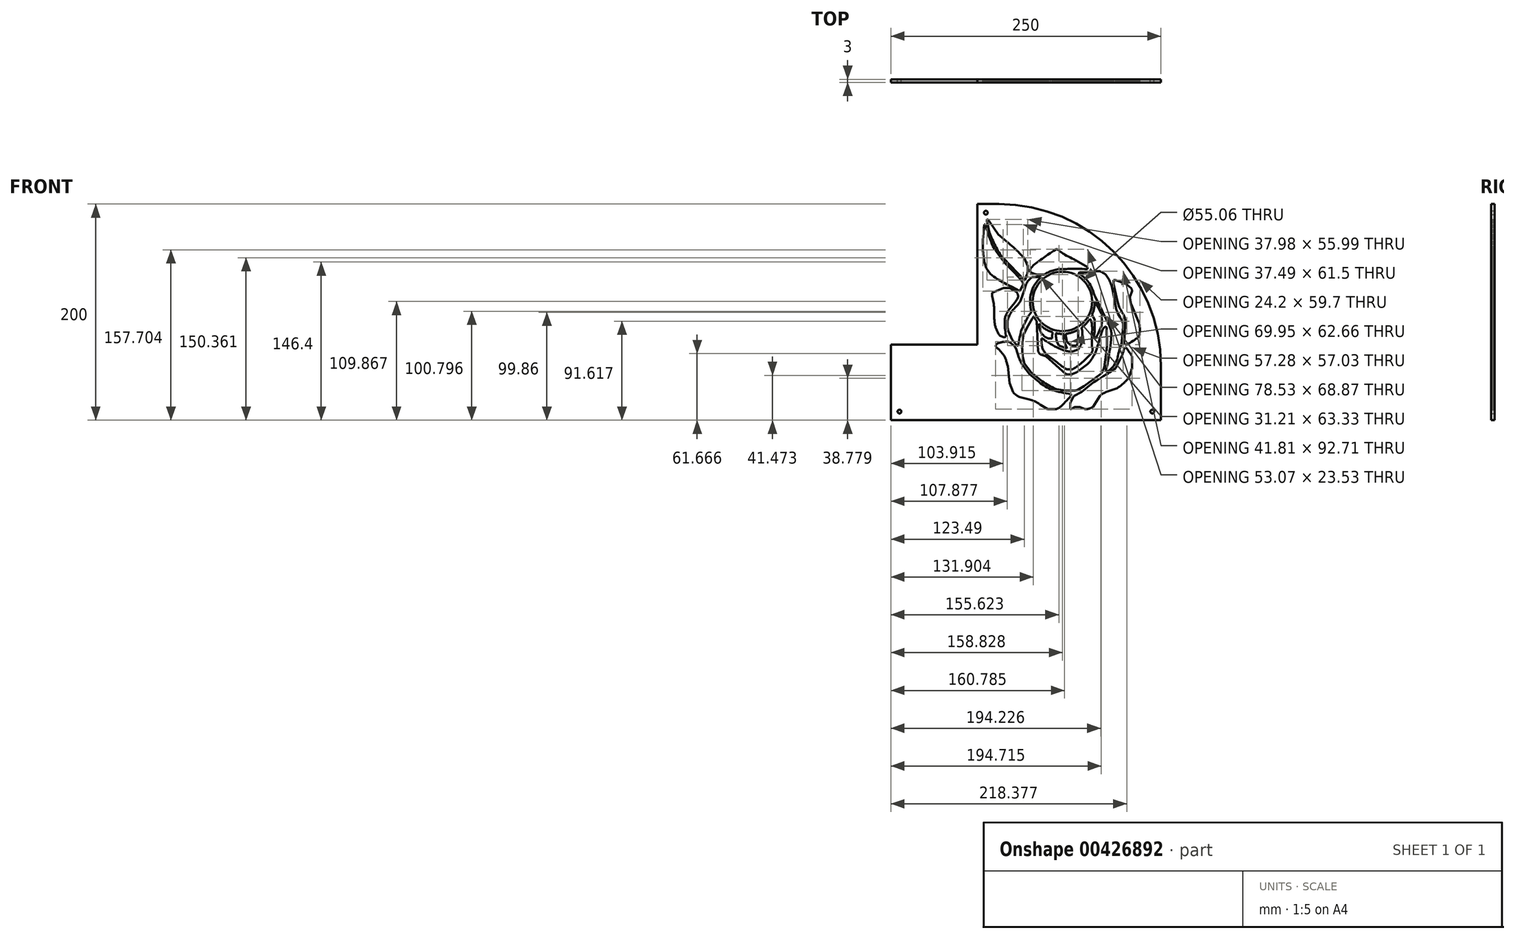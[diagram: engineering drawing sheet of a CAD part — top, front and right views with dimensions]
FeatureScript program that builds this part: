
annotation { "Feature Type Name" : "Feature", "Feature Type Description" : "" }
export const myFeature = defineFeature(function(context is Context, id is Id, definition is map)
    precondition{}
    {
        {
            var Q0;
            Q0=qCreatedBy(makeId("Front.planeOp"),FACE);
            var sketch = newSketch(context, id + "F0", { "sketchPlane" : qUnion([Q0])});
            skCircle(sketch, "E0", {"center": v(-37, 92) * mm, "radius": 1.75 * mm});
            skCircle(sketch, "E1", {"center": v(117, -92) * mm, "radius": 1.75 * mm});
            skCircle(sketch, "E2", {"center": v(-117, -92) * mm, "radius": 1.75 * mm});
            skArc(sketch, "E3", {"start": v(7.17, -3.9) * mm, "mid": v(8.49, -6.2) * mm, "end": v(10, -8.36) * mm});
            skArc(sketch, "E4", {"start": v(14.1, 32.46) * mm, "mid": v(4.86, 17.68) * mm, "end": v(5.4, 0.27) * mm});
            skArc(sketch, "E5", {"start": v(36.3, 39.77) * mm, "mid": v(26.32, 38.91) * mm, "end": v(17.19, 34.83) * mm});
            skArc(sketch, "E6", {"start": v(63.2, 15.94) * mm, "mid": v(57.98, 27.67) * mm, "end": v(48.32, 36.13) * mm});
            skArc(sketch, "E7", {"start": v(61.19, -2.44) * mm, "mid": v(63.17, 3.6) * mm, "end": v(63.83, 9.92) * mm});
            skArc(sketch, "E8", {"start": v(51.56, -14.33) * mm, "mid": v(55.76, -10.6) * mm, "end": v(59.19, -6.16) * mm});
            skArc(sketch, "E9", {"start": v(37.04, -19.96) * mm, "mid": v(42.76, -18.77) * mm, "end": v(48.14, -16.5) * mm});
            skArc(sketch, "E10", {"start": v(27.58, -19.48) * mm, "mid": v(31.5, -20.04) * mm, "end": v(35.45, -20.09) * mm});
            skArc(sketch, "E11", {"start": v(12.1, -10.82) * mm, "mid": v(17.92, -15.57) * mm, "end": v(24.74, -18.72) * mm});
            skLineSegment(sketch, "E12", {"start": v(-45, 100) * mm, "end": v(-25, 100) * mm});
            skLineSegment(sketch, "E13", {"start": v(-45, 100) * mm, "end": v(-45, -30) * mm});
            skLineSegment(sketch, "E14", {"start": v(-125, -30) * mm, "end": v(-45, -30) * mm});
            skLineSegment(sketch, "E15", {"start": v(-125, -100) * mm, "end": v(-125, -30) * mm});
            skLineSegment(sketch, "E16", {"start": v(-125, -100) * mm, "end": v(125, -100) * mm});
            skLineSegment(sketch, "E17", {"start": v(125, -100) * mm, "end": v(125, -50) * mm});
            skArc(sketch, "E18", {"start": v(125, -50) * mm, "mid": v(81.07, 56.07) * mm, "end": v(-25, 100) * mm});
            skLineSegment(sketch, "E19", {"start": v(-36.11, 85.7) * mm, "end": v(-35.91, 84.19) * mm});
            skLineSegment(sketch, "E20", {"start": v(-35.91, 84.19) * mm, "end": v(-35.68, 82.68) * mm});
            skLineSegment(sketch, "E21", {"start": v(-35.68, 82.68) * mm, "end": v(-35.43, 81.18) * mm});
            skLineSegment(sketch, "E22", {"start": v(-35.43, 81.18) * mm, "end": v(-35.14, 79.68) * mm});
            skLineSegment(sketch, "E23", {"start": v(-35.14, 79.68) * mm, "end": v(-34.83, 78.2) * mm});
            skLineSegment(sketch, "E24", {"start": v(-34.83, 78.2) * mm, "end": v(-34.49, 76.71) * mm});
            skLineSegment(sketch, "E25", {"start": v(-34.49, 76.71) * mm, "end": v(-34.11, 75.24) * mm});
            skLineSegment(sketch, "E26", {"start": v(-34.11, 75.24) * mm, "end": v(-33.7, 73.77) * mm});
            skLineSegment(sketch, "E27", {"start": v(-33.7, 73.77) * mm, "end": v(-32.43, 70.56) * mm});
            skLineSegment(sketch, "E28", {"start": v(-32.43, 70.56) * mm, "end": v(-31.78, 68.96) * mm});
            skLineSegment(sketch, "E29", {"start": v(-31.78, 68.96) * mm, "end": v(-31.11, 67.37) * mm});
            skLineSegment(sketch, "E30", {"start": v(-31.11, 67.37) * mm, "end": v(-30.43, 65.8) * mm});
            skLineSegment(sketch, "E31", {"start": v(-30.43, 65.8) * mm, "end": v(-29.72, 64.23) * mm});
            skLineSegment(sketch, "E32", {"start": v(-29.72, 64.23) * mm, "end": v(-28.99, 62.68) * mm});
            skLineSegment(sketch, "E33", {"start": v(-28.99, 62.68) * mm, "end": v(-28.23, 61.15) * mm});
            skLineSegment(sketch, "E34", {"start": v(-28.23, 61.15) * mm, "end": v(-27.44, 59.64) * mm});
            skLineSegment(sketch, "E35", {"start": v(-27.44, 59.64) * mm, "end": v(-26.62, 58.15) * mm});
            skLineSegment(sketch, "E36", {"start": v(-26.62, 58.15) * mm, "end": v(-25.76, 56.7) * mm});
            skLineSegment(sketch, "E37", {"start": v(-25.76, 56.7) * mm, "end": v(-24.86, 55.27) * mm});
            skLineSegment(sketch, "E38", {"start": v(-24.86, 55.27) * mm, "end": v(-23.93, 53.87) * mm});
            skLineSegment(sketch, "E39", {"start": v(-23.93, 53.87) * mm, "end": v(-22.94, 52.5) * mm});
            skLineSegment(sketch, "E40", {"start": v(-22.94, 52.5) * mm, "end": v(-22.44, 51.84) * mm});
            skLineSegment(sketch, "E41", {"start": v(-22.44, 51.84) * mm, "end": v(-21.91, 51.19) * mm});
            skLineSegment(sketch, "E42", {"start": v(-21.91, 51.19) * mm, "end": v(-21.38, 50.54) * mm});
            skLineSegment(sketch, "E43", {"start": v(-21.38, 50.54) * mm, "end": v(-20.84, 49.9) * mm});
            skLineSegment(sketch, "E44", {"start": v(-20.84, 49.9) * mm, "end": v(-1.54, 29.7) * mm});
            skLineSegment(sketch, "E45", {"start": v(-1.54, 29.7) * mm, "end": v(-0.73, 29.7) * mm});
            skLineSegment(sketch, "E46", {"start": v(-0.73, 29.7) * mm, "end": v(0.87, 34.3) * mm});
            skLineSegment(sketch, "E47", {"start": v(0.87, 34.3) * mm, "end": v(1.04, 34.79) * mm});
            skLineSegment(sketch, "E48", {"start": v(1.04, 34.79) * mm, "end": v(1.2, 35.28) * mm});
            skLineSegment(sketch, "E49", {"start": v(1.2, 35.28) * mm, "end": v(1.33, 35.78) * mm});
            skLineSegment(sketch, "E50", {"start": v(1.33, 35.78) * mm, "end": v(1.46, 36.3) * mm});
            skLineSegment(sketch, "E51", {"start": v(1.46, 36.3) * mm, "end": v(1.56, 36.8) * mm});
            skLineSegment(sketch, "E52", {"start": v(1.56, 36.8) * mm, "end": v(1.65, 37.32) * mm});
            skLineSegment(sketch, "E53", {"start": v(1.65, 37.32) * mm, "end": v(1.73, 37.84) * mm});
            skLineSegment(sketch, "E54", {"start": v(1.73, 37.84) * mm, "end": v(1.79, 38.36) * mm});
            skLineSegment(sketch, "E55", {"start": v(1.79, 38.36) * mm, "end": v(1.83, 38.89) * mm});
            skLineSegment(sketch, "E56", {"start": v(1.83, 38.89) * mm, "end": v(1.86, 39.41) * mm});
            skLineSegment(sketch, "E57", {"start": v(1.86, 39.41) * mm, "end": v(1.87, 39.94) * mm});
            skLineSegment(sketch, "E58", {"start": v(1.87, 39.94) * mm, "end": v(1.86, 40.47) * mm});
            skLineSegment(sketch, "E59", {"start": v(1.86, 40.47) * mm, "end": v(1.84, 41) * mm});
            skLineSegment(sketch, "E60", {"start": v(1.84, 41) * mm, "end": v(1.8, 41.52) * mm});
            skLineSegment(sketch, "E61", {"start": v(1.8, 41.52) * mm, "end": v(1.75, 42.04) * mm});
            skLineSegment(sketch, "E62", {"start": v(1.75, 42.04) * mm, "end": v(1.68, 42.56) * mm});
            skLineSegment(sketch, "E63", {"start": v(1.68, 42.56) * mm, "end": v(-1.54, 49.9) * mm});
            skLineSegment(sketch, "E64", {"start": v(-1.54, 49.9) * mm, "end": v(-2.92, 51.44) * mm});
            skLineSegment(sketch, "E65", {"start": v(-2.92, 51.44) * mm, "end": v(-4.32, 52.95) * mm});
            skLineSegment(sketch, "E66", {"start": v(-4.32, 52.95) * mm, "end": v(-5.75, 54.42) * mm});
            skLineSegment(sketch, "E67", {"start": v(-5.75, 54.42) * mm, "end": v(-7.2, 55.87) * mm});
            skLineSegment(sketch, "E68", {"start": v(-7.2, 55.87) * mm, "end": v(-8.67, 57.3) * mm});
            skLineSegment(sketch, "E69", {"start": v(-8.67, 57.3) * mm, "end": v(-10.16, 58.69) * mm});
            skLineSegment(sketch, "E70", {"start": v(-10.16, 58.69) * mm, "end": v(-11.67, 60.07) * mm});
            skLineSegment(sketch, "E71", {"start": v(-11.67, 60.07) * mm, "end": v(-13.19, 61.43) * mm});
            skLineSegment(sketch, "E72", {"start": v(-13.19, 61.43) * mm, "end": v(-14.72, 62.77) * mm});
            skLineSegment(sketch, "E73", {"start": v(-14.72, 62.77) * mm, "end": v(-16.27, 64.1) * mm});
            skLineSegment(sketch, "E74", {"start": v(-16.27, 64.1) * mm, "end": v(-19.39, 66.73) * mm});
            skLineSegment(sketch, "E75", {"start": v(-19.39, 66.73) * mm, "end": v(-25.66, 71.93) * mm});
            skLineSegment(sketch, "E76", {"start": v(-25.66, 71.93) * mm, "end": v(-33.7, 83.86) * mm});
            skLineSegment(sketch, "E77", {"start": v(-33.7, 83.86) * mm, "end": v(-34.12, 84.53) * mm});
            skLineSegment(sketch, "E78", {"start": v(-34.12, 84.53) * mm, "end": v(-34.34, 84.84) * mm});
            skLineSegment(sketch, "E79", {"start": v(-34.34, 84.84) * mm, "end": v(-34.6, 85.12) * mm});
            skLineSegment(sketch, "E80", {"start": v(-34.6, 85.12) * mm, "end": v(-34.73, 85.24) * mm});
            skLineSegment(sketch, "E81", {"start": v(-34.73, 85.24) * mm, "end": v(-34.88, 85.35) * mm});
            skLineSegment(sketch, "E82", {"start": v(-34.88, 85.35) * mm, "end": v(-35.04, 85.45) * mm});
            skLineSegment(sketch, "E83", {"start": v(-35.04, 85.45) * mm, "end": v(-35.22, 85.54) * mm});
            skLineSegment(sketch, "E84", {"start": v(-35.22, 85.54) * mm, "end": v(-35.41, 85.6) * mm});
            skLineSegment(sketch, "E85", {"start": v(-35.41, 85.6) * mm, "end": v(-35.63, 85.66) * mm});
            skLineSegment(sketch, "E86", {"start": v(-35.63, 85.66) * mm, "end": v(-35.86, 85.69) * mm});
            skLineSegment(sketch, "E87", {"start": v(-35.86, 85.69) * mm, "end": v(-36.11, 85.7) * mm});
            skLineSegment(sketch, "E88", {"start": v(-37.72, 81.11) * mm, "end": v(-38.52, 81.11) * mm});
            skLineSegment(sketch, "E89", {"start": v(-38.52, 81.11) * mm, "end": v(-39.33, 73.77) * mm});
            skLineSegment(sketch, "E90", {"start": v(-39.33, 73.77) * mm, "end": v(-39.58, 69.44) * mm});
            skLineSegment(sketch, "E91", {"start": v(-39.58, 69.44) * mm, "end": v(-39.68, 67.27) * mm});
            skLineSegment(sketch, "E92", {"start": v(-39.68, 67.27) * mm, "end": v(-39.77, 65.09) * mm});
            skLineSegment(sketch, "E93", {"start": v(-39.77, 65.09) * mm, "end": v(-39.82, 62.91) * mm});
            skLineSegment(sketch, "E94", {"start": v(-39.82, 62.91) * mm, "end": v(-39.83, 60.74) * mm});
            skLineSegment(sketch, "E95", {"start": v(-39.83, 60.74) * mm, "end": v(-39.8, 58.57) * mm});
            skLineSegment(sketch, "E96", {"start": v(-39.8, 58.57) * mm, "end": v(-39.7, 56.4) * mm});
            skLineSegment(sketch, "E97", {"start": v(-39.7, 56.4) * mm, "end": v(-39.64, 55.33) * mm});
            skLineSegment(sketch, "E98", {"start": v(-39.64, 55.33) * mm, "end": v(-39.55, 54.26) * mm});
            skLineSegment(sketch, "E99", {"start": v(-39.55, 54.26) * mm, "end": v(-39.45, 53.19) * mm});
            skLineSegment(sketch, "E100", {"start": v(-39.45, 53.19) * mm, "end": v(-39.33, 52.13) * mm});
            skLineSegment(sketch, "E101", {"start": v(-39.33, 52.13) * mm, "end": v(-39.2, 51.07) * mm});
            skLineSegment(sketch, "E102", {"start": v(-39.2, 51.07) * mm, "end": v(-39.03, 50) * mm});
            skLineSegment(sketch, "E103", {"start": v(-39.03, 50) * mm, "end": v(-38.85, 48.96) * mm});
            skLineSegment(sketch, "E104", {"start": v(-38.85, 48.96) * mm, "end": v(-38.65, 47.92) * mm});
            skLineSegment(sketch, "E105", {"start": v(-38.65, 47.92) * mm, "end": v(-38.42, 46.88) * mm});
            skLineSegment(sketch, "E106", {"start": v(-38.42, 46.88) * mm, "end": v(-38.17, 45.84) * mm});
            skLineSegment(sketch, "E107", {"start": v(-38.17, 45.84) * mm, "end": v(-37.9, 44.82) * mm});
            skLineSegment(sketch, "E108", {"start": v(-37.9, 44.82) * mm, "end": v(-37.6, 43.8) * mm});
            skLineSegment(sketch, "E109", {"start": v(-37.6, 43.8) * mm, "end": v(-37.27, 42.8) * mm});
            skLineSegment(sketch, "E110", {"start": v(-37.27, 42.8) * mm, "end": v(-36.91, 41.79) * mm});
            skLineSegment(sketch, "E111", {"start": v(-36.91, 41.79) * mm, "end": v(-36.53, 40.8) * mm});
            skLineSegment(sketch, "E112", {"start": v(-36.53, 40.8) * mm, "end": v(-36.11, 39.8) * mm});
            skLineSegment(sketch, "E113", {"start": v(-36.11, 39.8) * mm, "end": v(-32.9, 35.22) * mm});
            skLineSegment(sketch, "E114", {"start": v(-32.9, 35.22) * mm, "end": v(-31.3, 34.03) * mm});
            skLineSegment(sketch, "E115", {"start": v(-31.3, 34.03) * mm, "end": v(-29.67, 32.9) * mm});
            skLineSegment(sketch, "E116", {"start": v(-29.67, 32.9) * mm, "end": v(-28.03, 31.8) * mm});
            skLineSegment(sketch, "E117", {"start": v(-28.03, 31.8) * mm, "end": v(-26.36, 30.73) * mm});
            skLineSegment(sketch, "E118", {"start": v(-26.36, 30.73) * mm, "end": v(-24.68, 29.7) * mm});
            skLineSegment(sketch, "E119", {"start": v(-24.68, 29.7) * mm, "end": v(-22.98, 28.7) * mm});
            skLineSegment(sketch, "E120", {"start": v(-22.98, 28.7) * mm, "end": v(-21.27, 27.74) * mm});
            skLineSegment(sketch, "E121", {"start": v(-21.27, 27.74) * mm, "end": v(-19.55, 26.8) * mm});
            skLineSegment(sketch, "E122", {"start": v(-19.55, 26.8) * mm, "end": v(-17.81, 25.87) * mm});
            skLineSegment(sketch, "E123", {"start": v(-17.81, 25.87) * mm, "end": v(-16.07, 24.95) * mm});
            skLineSegment(sketch, "E124", {"start": v(-16.07, 24.95) * mm, "end": v(-12.57, 23.16) * mm});
            skLineSegment(sketch, "E125", {"start": v(-12.57, 23.16) * mm, "end": v(-9.06, 21.4) * mm});
            skLineSegment(sketch, "E126", {"start": v(-9.06, 21.4) * mm, "end": v(-5.56, 19.61) * mm});
            skLineSegment(sketch, "E127", {"start": v(-5.56, 19.61) * mm, "end": v(-2.34, 26.04) * mm});
            skLineSegment(sketch, "E128", {"start": v(-2.34, 26.04) * mm, "end": v(-3.15, 27.87) * mm});
            skLineSegment(sketch, "E129", {"start": v(-3.15, 27.87) * mm, "end": v(-3.98, 28.93) * mm});
            skLineSegment(sketch, "E130", {"start": v(-3.98, 28.93) * mm, "end": v(-4.82, 29.97) * mm});
            skLineSegment(sketch, "E131", {"start": v(-4.82, 29.97) * mm, "end": v(-6.53, 32.03) * mm});
            skLineSegment(sketch, "E132", {"start": v(-6.53, 32.03) * mm, "end": v(-8.29, 34.04) * mm});
            skLineSegment(sketch, "E133", {"start": v(-8.29, 34.04) * mm, "end": v(-10.08, 36.01) * mm});
            skLineSegment(sketch, "E134", {"start": v(-10.08, 36.01) * mm, "end": v(-11.9, 37.94) * mm});
            skLineSegment(sketch, "E135", {"start": v(-11.9, 37.94) * mm, "end": v(-13.78, 39.83) * mm});
            skLineSegment(sketch, "E136", {"start": v(-13.78, 39.83) * mm, "end": v(-15.68, 41.67) * mm});
            skLineSegment(sketch, "E137", {"start": v(-15.68, 41.67) * mm, "end": v(-17.62, 43.48) * mm});
            skLineSegment(sketch, "E138", {"start": v(-17.62, 43.48) * mm, "end": v(-18.5, 44.5) * mm});
            skLineSegment(sketch, "E139", {"start": v(-18.5, 44.5) * mm, "end": v(-19.36, 45.52) * mm});
            skLineSegment(sketch, "E140", {"start": v(-19.36, 45.52) * mm, "end": v(-20.22, 46.55) * mm});
            skLineSegment(sketch, "E141", {"start": v(-20.22, 46.55) * mm, "end": v(-21.06, 47.6) * mm});
            skLineSegment(sketch, "E142", {"start": v(-21.06, 47.6) * mm, "end": v(-22.72, 49.73) * mm});
            skLineSegment(sketch, "E143", {"start": v(-22.72, 49.73) * mm, "end": v(-24.34, 51.9) * mm});
            skLineSegment(sketch, "E144", {"start": v(-24.34, 51.9) * mm, "end": v(-25.92, 54.1) * mm});
            skLineSegment(sketch, "E145", {"start": v(-25.92, 54.1) * mm, "end": v(-27.47, 56.34) * mm});
            skLineSegment(sketch, "E146", {"start": v(-27.47, 56.34) * mm, "end": v(-29, 58.61) * mm});
            skLineSegment(sketch, "E147", {"start": v(-29, 58.61) * mm, "end": v(-30.48, 60.92) * mm});
            skLineSegment(sketch, "E148", {"start": v(-30.48, 60.92) * mm, "end": v(-31.43, 63.14) * mm});
            skLineSegment(sketch, "E149", {"start": v(-31.43, 63.14) * mm, "end": v(-32.32, 65.39) * mm});
            skLineSegment(sketch, "E150", {"start": v(-32.32, 65.39) * mm, "end": v(-33.17, 67.66) * mm});
            skLineSegment(sketch, "E151", {"start": v(-33.17, 67.66) * mm, "end": v(-33.98, 69.95) * mm});
            skLineSegment(sketch, "E152", {"start": v(-33.98, 69.95) * mm, "end": v(-34.76, 72.26) * mm});
            skLineSegment(sketch, "E153", {"start": v(-34.76, 72.26) * mm, "end": v(-35.5, 74.59) * mm});
            skLineSegment(sketch, "E154", {"start": v(-35.5, 74.59) * mm, "end": v(-36.22, 76.92) * mm});
            skLineSegment(sketch, "E155", {"start": v(-36.22, 76.92) * mm, "end": v(-36.92, 79.27) * mm});
            skLineSegment(sketch, "E156", {"start": v(-36.92, 79.27) * mm, "end": v(-37.72, 81.11) * mm});
            skLineSegment(sketch, "E157", {"start": v(36.3, 39.77) * mm, "end": v(37.58, 39.94) * mm});
            skLineSegment(sketch, "E158", {"start": v(37.58, 39.94) * mm, "end": v(38.87, 40.06) * mm});
            skLineSegment(sketch, "E159", {"start": v(38.87, 40.06) * mm, "end": v(40.16, 40.15) * mm});
            skLineSegment(sketch, "E160", {"start": v(40.16, 40.15) * mm, "end": v(41.46, 40.2) * mm});
            skLineSegment(sketch, "E161", {"start": v(41.46, 40.2) * mm, "end": v(42.76, 40.23) * mm});
            skLineSegment(sketch, "E162", {"start": v(42.76, 40.23) * mm, "end": v(44.07, 40.23) * mm});
            skLineSegment(sketch, "E163", {"start": v(44.07, 40.23) * mm, "end": v(45.37, 40.2) * mm});
            skLineSegment(sketch, "E164", {"start": v(45.37, 40.2) * mm, "end": v(46.68, 40.17) * mm});
            skLineSegment(sketch, "E165", {"start": v(46.68, 40.17) * mm, "end": v(49.3, 40.06) * mm});
            skLineSegment(sketch, "E166", {"start": v(49.3, 40.06) * mm, "end": v(51.93, 39.94) * mm});
            skLineSegment(sketch, "E167", {"start": v(51.93, 39.94) * mm, "end": v(54.55, 39.85) * mm});
            skLineSegment(sketch, "E168", {"start": v(54.55, 39.85) * mm, "end": v(55.85, 39.82) * mm});
            skLineSegment(sketch, "E169", {"start": v(55.85, 39.82) * mm, "end": v(57.16, 39.8) * mm});
            skLineSegment(sketch, "E170", {"start": v(57.16, 39.8) * mm, "end": v(57.16, 41.64) * mm});
            skLineSegment(sketch, "E171", {"start": v(57.16, 41.64) * mm, "end": v(44.3, 48.98) * mm});
            skLineSegment(sketch, "E172", {"start": v(44.3, 48.98) * mm, "end": v(42.63, 49.76) * mm});
            skLineSegment(sketch, "E173", {"start": v(42.63, 49.76) * mm, "end": v(40.97, 50.56) * mm});
            skLineSegment(sketch, "E174", {"start": v(40.97, 50.56) * mm, "end": v(39.33, 51.4) * mm});
            skLineSegment(sketch, "E175", {"start": v(39.33, 51.4) * mm, "end": v(37.7, 52.26) * mm});
            skLineSegment(sketch, "E176", {"start": v(37.7, 52.26) * mm, "end": v(36.1, 53.19) * mm});
            skLineSegment(sketch, "E177", {"start": v(36.1, 53.19) * mm, "end": v(35.3, 53.67) * mm});
            skLineSegment(sketch, "E178", {"start": v(35.3, 53.67) * mm, "end": v(34.52, 54.17) * mm});
            skLineSegment(sketch, "E179", {"start": v(34.52, 54.17) * mm, "end": v(33.73, 54.68) * mm});
            skLineSegment(sketch, "E180", {"start": v(33.73, 54.68) * mm, "end": v(32.96, 55.21) * mm});
            skLineSegment(sketch, "E181", {"start": v(32.96, 55.21) * mm, "end": v(32.19, 55.76) * mm});
            skLineSegment(sketch, "E182", {"start": v(32.19, 55.76) * mm, "end": v(31.43, 56.33) * mm});
            skLineSegment(sketch, "E183", {"start": v(31.43, 56.33) * mm, "end": v(31.1, 56.68) * mm});
            skLineSegment(sketch, "E184", {"start": v(31.1, 56.68) * mm, "end": v(30.77, 57.02) * mm});
            skLineSegment(sketch, "E185", {"start": v(30.77, 57.02) * mm, "end": v(30.42, 57.33) * mm});
            skLineSegment(sketch, "E186", {"start": v(30.42, 57.33) * mm, "end": v(30.05, 57.6) * mm});
            skLineSegment(sketch, "E187", {"start": v(30.05, 57.6) * mm, "end": v(29.85, 57.73) * mm});
            skLineSegment(sketch, "E188", {"start": v(29.85, 57.73) * mm, "end": v(29.65, 57.84) * mm});
            skLineSegment(sketch, "E189", {"start": v(29.65, 57.84) * mm, "end": v(29.43, 57.93) * mm});
            skLineSegment(sketch, "E190", {"start": v(29.43, 57.93) * mm, "end": v(29.2, 58.01) * mm});
            skLineSegment(sketch, "E191", {"start": v(29.2, 58.01) * mm, "end": v(28.98, 58.08) * mm});
            skLineSegment(sketch, "E192", {"start": v(28.98, 58.08) * mm, "end": v(28.73, 58.12) * mm});
            skLineSegment(sketch, "E193", {"start": v(28.73, 58.12) * mm, "end": v(28.48, 58.15) * mm});
            skLineSegment(sketch, "E194", {"start": v(28.48, 58.15) * mm, "end": v(28.21, 58.16) * mm});
            skLineSegment(sketch, "E195", {"start": v(28.21, 58.16) * mm, "end": v(25.51, 56.5) * mm});
            skLineSegment(sketch, "E196", {"start": v(25.51, 56.5) * mm, "end": v(22.83, 54.8) * mm});
            skLineSegment(sketch, "E197", {"start": v(22.83, 54.8) * mm, "end": v(20.18, 53.04) * mm});
            skLineSegment(sketch, "E198", {"start": v(20.18, 53.04) * mm, "end": v(17.55, 51.24) * mm});
            skLineSegment(sketch, "E199", {"start": v(17.55, 51.24) * mm, "end": v(16.24, 50.32) * mm});
            skLineSegment(sketch, "E200", {"start": v(16.24, 50.32) * mm, "end": v(14.94, 49.4) * mm});
            skLineSegment(sketch, "E201", {"start": v(14.94, 49.4) * mm, "end": v(13.65, 48.45) * mm});
            skLineSegment(sketch, "E202", {"start": v(13.65, 48.45) * mm, "end": v(12.36, 47.48) * mm});
            skLineSegment(sketch, "E203", {"start": v(12.36, 47.48) * mm, "end": v(11.09, 46.5) * mm});
            skLineSegment(sketch, "E204", {"start": v(11.09, 46.5) * mm, "end": v(9.82, 45.51) * mm});
            skLineSegment(sketch, "E205", {"start": v(9.82, 45.51) * mm, "end": v(8.56, 44.5) * mm});
            skLineSegment(sketch, "E206", {"start": v(8.56, 44.5) * mm, "end": v(7.3, 43.48) * mm});
            skLineSegment(sketch, "E207", {"start": v(7.3, 43.48) * mm, "end": v(4.09, 39.8) * mm});
            skLineSegment(sketch, "E208", {"start": v(4.09, 39.8) * mm, "end": v(4.09, 37.05) * mm});
            skLineSegment(sketch, "E209", {"start": v(4.09, 37.05) * mm, "end": v(8.11, 35.22) * mm});
            skLineSegment(sketch, "E210", {"start": v(8.11, 35.22) * mm, "end": v(9.24, 35) * mm});
            skLineSegment(sketch, "E211", {"start": v(9.24, 35) * mm, "end": v(10.37, 34.84) * mm});
            skLineSegment(sketch, "E212", {"start": v(10.37, 34.84) * mm, "end": v(11.5, 34.72) * mm});
            skLineSegment(sketch, "E213", {"start": v(11.5, 34.72) * mm, "end": v(12.64, 34.66) * mm});
            skLineSegment(sketch, "E214", {"start": v(12.64, 34.66) * mm, "end": v(13.77, 34.64) * mm});
            skLineSegment(sketch, "E215", {"start": v(13.77, 34.64) * mm, "end": v(14.91, 34.66) * mm});
            skLineSegment(sketch, "E216", {"start": v(14.91, 34.66) * mm, "end": v(16.05, 34.73) * mm});
            skLineSegment(sketch, "E217", {"start": v(16.05, 34.73) * mm, "end": v(17.19, 34.83) * mm});
            skLineSegment(sketch, "E218", {"start": v(63.2, 15.94) * mm, "end": v(64.4, 14.1) * mm});
            skLineSegment(sketch, "E219", {"start": v(64.4, 14.1) * mm, "end": v(77.26, -12.51) * mm});
            skLineSegment(sketch, "E220", {"start": v(77.26, -12.51) * mm, "end": v(78.87, -17.1) * mm});
            skLineSegment(sketch, "E221", {"start": v(78.87, -17.1) * mm, "end": v(79, -18.12) * mm});
            skLineSegment(sketch, "E222", {"start": v(79, -18.12) * mm, "end": v(79.07, -19.15) * mm});
            skLineSegment(sketch, "E223", {"start": v(79.07, -19.15) * mm, "end": v(79.1, -20.18) * mm});
            skLineSegment(sketch, "E224", {"start": v(79.1, -20.18) * mm, "end": v(79.1, -21.22) * mm});
            skLineSegment(sketch, "E225", {"start": v(79.1, -21.22) * mm, "end": v(79.07, -22.26) * mm});
            skLineSegment(sketch, "E226", {"start": v(79.07, -22.26) * mm, "end": v(79.01, -23.3) * mm});
            skLineSegment(sketch, "E227", {"start": v(79.01, -23.3) * mm, "end": v(78.87, -25.36) * mm});
            skLineSegment(sketch, "E228", {"start": v(78.87, -25.36) * mm, "end": v(78.2, -30.9) * mm});
            skLineSegment(sketch, "E229", {"start": v(78.2, -30.9) * mm, "end": v(77.84, -33.66) * mm});
            skLineSegment(sketch, "E230", {"start": v(77.84, -33.66) * mm, "end": v(77.47, -36.41) * mm});
            skLineSegment(sketch, "E231", {"start": v(77.47, -36.41) * mm, "end": v(77.06, -39.17) * mm});
            skLineSegment(sketch, "E232", {"start": v(77.06, -39.17) * mm, "end": v(76.63, -41.92) * mm});
            skLineSegment(sketch, "E233", {"start": v(76.63, -41.92) * mm, "end": v(76.16, -44.66) * mm});
            skLineSegment(sketch, "E234", {"start": v(76.16, -44.66) * mm, "end": v(75.65, -47.4) * mm});
            skLineSegment(sketch, "E235", {"start": v(75.65, -47.4) * mm, "end": v(74.04, -52.9) * mm});
            skLineSegment(sketch, "E236", {"start": v(74.04, -52.9) * mm, "end": v(74.04, -54.74) * mm});
            skLineSegment(sketch, "E237", {"start": v(74.04, -54.74) * mm, "end": v(74.46, -54.73) * mm});
            skLineSegment(sketch, "E238", {"start": v(74.46, -54.73) * mm, "end": v(74.88, -54.7) * mm});
            skLineSegment(sketch, "E239", {"start": v(74.88, -54.7) * mm, "end": v(75.3, -54.65) * mm});
            skLineSegment(sketch, "E240", {"start": v(75.3, -54.65) * mm, "end": v(75.71, -54.57) * mm});
            skLineSegment(sketch, "E241", {"start": v(75.71, -54.57) * mm, "end": v(76.12, -54.45) * mm});
            skLineSegment(sketch, "E242", {"start": v(76.12, -54.45) * mm, "end": v(76.51, -54.3) * mm});
            skLineSegment(sketch, "E243", {"start": v(76.51, -54.3) * mm, "end": v(76.9, -54.08) * mm});
            skLineSegment(sketch, "E244", {"start": v(76.9, -54.08) * mm, "end": v(77.26, -53.82) * mm});
            skLineSegment(sketch, "E245", {"start": v(77.26, -53.82) * mm, "end": v(81.28, -50.15) * mm});
            skLineSegment(sketch, "E246", {"start": v(81.28, -50.15) * mm, "end": v(84.5, -43.72) * mm});
            skLineSegment(sketch, "E247", {"start": v(84.5, -43.72) * mm, "end": v(84.88, -41.96) * mm});
            skLineSegment(sketch, "E248", {"start": v(84.88, -41.96) * mm, "end": v(85.29, -40.2) * mm});
            skLineSegment(sketch, "E249", {"start": v(85.29, -40.2) * mm, "end": v(85.71, -38.45) * mm});
            skLineSegment(sketch, "E250", {"start": v(85.71, -38.45) * mm, "end": v(86.17, -36.71) * mm});
            skLineSegment(sketch, "E251", {"start": v(86.17, -36.71) * mm, "end": v(86.67, -34.99) * mm});
            skLineSegment(sketch, "E252", {"start": v(86.67, -34.99) * mm, "end": v(86.94, -34.13) * mm});
            skLineSegment(sketch, "E253", {"start": v(86.94, -34.13) * mm, "end": v(87.22, -33.29) * mm});
            skLineSegment(sketch, "E254", {"start": v(87.22, -33.29) * mm, "end": v(87.52, -32.44) * mm});
            skLineSegment(sketch, "E255", {"start": v(87.52, -32.44) * mm, "end": v(87.83, -31.6) * mm});
            skLineSegment(sketch, "E256", {"start": v(87.83, -31.6) * mm, "end": v(88.17, -30.78) * mm});
            skLineSegment(sketch, "E257", {"start": v(88.17, -30.78) * mm, "end": v(88.51, -29.95) * mm});
            skLineSegment(sketch, "E258", {"start": v(88.51, -29.95) * mm, "end": v(90.12, -13.43) * mm});
            skLineSegment(sketch, "E259", {"start": v(90.12, -13.43) * mm, "end": v(90.13, -12.97) * mm});
            skLineSegment(sketch, "E260", {"start": v(90.13, -12.97) * mm, "end": v(90.12, -12.52) * mm});
            skLineSegment(sketch, "E261", {"start": v(90.12, -12.52) * mm, "end": v(90.09, -12.07) * mm});
            skLineSegment(sketch, "E262", {"start": v(90.09, -12.07) * mm, "end": v(90.03, -11.62) * mm});
            skLineSegment(sketch, "E263", {"start": v(90.03, -11.62) * mm, "end": v(89.96, -11.18) * mm});
            skLineSegment(sketch, "E264", {"start": v(89.96, -11.18) * mm, "end": v(89.88, -10.74) * mm});
            skLineSegment(sketch, "E265", {"start": v(89.88, -10.74) * mm, "end": v(89.77, -10.3) * mm});
            skLineSegment(sketch, "E266", {"start": v(89.77, -10.3) * mm, "end": v(89.65, -9.86) * mm});
            skLineSegment(sketch, "E267", {"start": v(89.65, -9.86) * mm, "end": v(89.37, -8.99) * mm});
            skLineSegment(sketch, "E268", {"start": v(89.37, -8.99) * mm, "end": v(89.04, -8.13) * mm});
            skLineSegment(sketch, "E269", {"start": v(89.04, -8.13) * mm, "end": v(88.66, -7.27) * mm});
            skLineSegment(sketch, "E270", {"start": v(88.66, -7.27) * mm, "end": v(88.24, -6.42) * mm});
            skLineSegment(sketch, "E271", {"start": v(88.24, -6.42) * mm, "end": v(87.8, -5.57) * mm});
            skLineSegment(sketch, "E272", {"start": v(87.8, -5.57) * mm, "end": v(87.33, -4.73) * mm});
            skLineSegment(sketch, "E273", {"start": v(87.33, -4.73) * mm, "end": v(86.36, -3.05) * mm});
            skLineSegment(sketch, "E274", {"start": v(86.36, -3.05) * mm, "end": v(85.4, -1.36) * mm});
            skLineSegment(sketch, "E275", {"start": v(85.4, -1.36) * mm, "end": v(84.94, -0.51) * mm});
            skLineSegment(sketch, "E276", {"start": v(84.94, -0.51) * mm, "end": v(84.5, 0.34) * mm});
            skLineSegment(sketch, "E277", {"start": v(84.5, 0.34) * mm, "end": v(83.7, 2.17) * mm});
            skLineSegment(sketch, "E278", {"start": v(83.7, 2.17) * mm, "end": v(80.47, 19.61) * mm});
            skLineSegment(sketch, "E279", {"start": v(80.47, 19.61) * mm, "end": v(79.8, 22.19) * mm});
            skLineSegment(sketch, "E280", {"start": v(79.8, 22.19) * mm, "end": v(79.45, 23.47) * mm});
            skLineSegment(sketch, "E281", {"start": v(79.45, 23.47) * mm, "end": v(79.07, 24.74) * mm});
            skLineSegment(sketch, "E282", {"start": v(79.07, 24.74) * mm, "end": v(78.67, 26) * mm});
            skLineSegment(sketch, "E283", {"start": v(78.67, 26) * mm, "end": v(78.24, 27.25) * mm});
            skLineSegment(sketch, "E284", {"start": v(78.24, 27.25) * mm, "end": v(77.77, 28.49) * mm});
            skLineSegment(sketch, "E285", {"start": v(77.77, 28.49) * mm, "end": v(77.26, 29.7) * mm});
            skLineSegment(sketch, "E286", {"start": v(77.26, 29.7) * mm, "end": v(74.04, 34.3) * mm});
            skLineSegment(sketch, "E287", {"start": v(74.04, 34.3) * mm, "end": v(73.75, 34.62) * mm});
            skLineSegment(sketch, "E288", {"start": v(73.75, 34.62) * mm, "end": v(73.45, 34.92) * mm});
            skLineSegment(sketch, "E289", {"start": v(73.45, 34.92) * mm, "end": v(73.13, 35.2) * mm});
            skLineSegment(sketch, "E290", {"start": v(73.13, 35.2) * mm, "end": v(72.8, 35.48) * mm});
            skLineSegment(sketch, "E291", {"start": v(72.8, 35.48) * mm, "end": v(72.47, 35.73) * mm});
            skLineSegment(sketch, "E292", {"start": v(72.47, 35.73) * mm, "end": v(72.13, 35.98) * mm});
            skLineSegment(sketch, "E293", {"start": v(72.13, 35.98) * mm, "end": v(71.43, 36.43) * mm});
            skLineSegment(sketch, "E294", {"start": v(71.43, 36.43) * mm, "end": v(70.7, 36.85) * mm});
            skLineSegment(sketch, "E295", {"start": v(70.7, 36.85) * mm, "end": v(69.95, 37.24) * mm});
            skLineSegment(sketch, "E296", {"start": v(69.95, 37.24) * mm, "end": v(69.19, 37.61) * mm});
            skLineSegment(sketch, "E297", {"start": v(69.19, 37.61) * mm, "end": v(68.41, 37.97) * mm});
            skLineSegment(sketch, "E298", {"start": v(68.41, 37.97) * mm, "end": v(63.59, 37.97) * mm});
            skLineSegment(sketch, "E299", {"start": v(63.59, 37.97) * mm, "end": v(61.7, 37.62) * mm});
            skLineSegment(sketch, "E300", {"start": v(61.7, 37.62) * mm, "end": v(59.8, 37.28) * mm});
            skLineSegment(sketch, "E301", {"start": v(59.8, 37.28) * mm, "end": v(57.9, 36.97) * mm});
            skLineSegment(sketch, "E302", {"start": v(57.9, 36.97) * mm, "end": v(56, 36.7) * mm});
            skLineSegment(sketch, "E303", {"start": v(56, 36.7) * mm, "end": v(54.09, 36.46) * mm});
            skLineSegment(sketch, "E304", {"start": v(54.09, 36.46) * mm, "end": v(53.13, 36.37) * mm});
            skLineSegment(sketch, "E305", {"start": v(53.13, 36.37) * mm, "end": v(52.17, 36.29) * mm});
            skLineSegment(sketch, "E306", {"start": v(52.17, 36.29) * mm, "end": v(51.21, 36.22) * mm});
            skLineSegment(sketch, "E307", {"start": v(51.21, 36.22) * mm, "end": v(50.25, 36.17) * mm});
            skLineSegment(sketch, "E308", {"start": v(50.25, 36.17) * mm, "end": v(49.29, 36.14) * mm});
            skLineSegment(sketch, "E309", {"start": v(49.29, 36.14) * mm, "end": v(48.32, 36.13) * mm});
            skLineSegment(sketch, "E310", {"start": v(14.1, 32.46) * mm, "end": v(5.7, 32.46) * mm});
            skLineSegment(sketch, "E311", {"start": v(5.7, 32.46) * mm, "end": v(1.68, 28.8) * mm});
            skLineSegment(sketch, "E312", {"start": v(1.68, 28.8) * mm, "end": v(1.15, 27.84) * mm});
            skLineSegment(sketch, "E313", {"start": v(1.15, 27.84) * mm, "end": v(0.68, 26.85) * mm});
            skLineSegment(sketch, "E314", {"start": v(0.68, 26.85) * mm, "end": v(0.24, 25.84) * mm});
            skLineSegment(sketch, "E315", {"start": v(0.24, 25.84) * mm, "end": v(-0.16, 24.8) * mm});
            skLineSegment(sketch, "E316", {"start": v(-0.16, 24.8) * mm, "end": v(-0.54, 23.76) * mm});
            skLineSegment(sketch, "E317", {"start": v(-0.54, 23.76) * mm, "end": v(-0.89, 22.7) * mm});
            skLineSegment(sketch, "E318", {"start": v(-0.89, 22.7) * mm, "end": v(-1.22, 21.61) * mm});
            skLineSegment(sketch, "E319", {"start": v(-1.22, 21.61) * mm, "end": v(-1.54, 20.53) * mm});
            skLineSegment(sketch, "E320", {"start": v(-1.54, 20.53) * mm, "end": v(-4.75, 10.43) * mm});
            skLineSegment(sketch, "E321", {"start": v(-4.75, 10.43) * mm, "end": v(-5.57, 9.3) * mm});
            skLineSegment(sketch, "E322", {"start": v(-5.57, 9.3) * mm, "end": v(-6.4, 8.2) * mm});
            skLineSegment(sketch, "E323", {"start": v(-6.4, 8.2) * mm, "end": v(-7.27, 7.13) * mm});
            skLineSegment(sketch, "E324", {"start": v(-7.27, 7.13) * mm, "end": v(-8.16, 6.09) * mm});
            skLineSegment(sketch, "E325", {"start": v(-8.16, 6.09) * mm, "end": v(-9.08, 5.07) * mm});
            skLineSegment(sketch, "E326", {"start": v(-9.08, 5.07) * mm, "end": v(-10.02, 4.08) * mm});
            skLineSegment(sketch, "E327", {"start": v(-10.02, 4.08) * mm, "end": v(-11, 3.11) * mm});
            skLineSegment(sketch, "E328", {"start": v(-11, 3.11) * mm, "end": v(-12, 2.17) * mm});
            skLineSegment(sketch, "E329", {"start": v(-12, 2.17) * mm, "end": v(-12.71, 1.12) * mm});
            skLineSegment(sketch, "E330", {"start": v(-12.71, 1.12) * mm, "end": v(-13.4, 0.04) * mm});
            skLineSegment(sketch, "E331", {"start": v(-13.4, 0.04) * mm, "end": v(-14.06, -1.06) * mm});
            skLineSegment(sketch, "E332", {"start": v(-14.06, -1.06) * mm, "end": v(-14.69, -2.19) * mm});
            skLineSegment(sketch, "E333", {"start": v(-14.69, -2.19) * mm, "end": v(-15.28, -3.35) * mm});
            skLineSegment(sketch, "E334", {"start": v(-15.28, -3.35) * mm, "end": v(-15.83, -4.53) * mm});
            skLineSegment(sketch, "E335", {"start": v(-15.83, -4.53) * mm, "end": v(-16.35, -5.75) * mm});
            skLineSegment(sketch, "E336", {"start": v(-16.35, -5.75) * mm, "end": v(-16.82, -7) * mm});
            skLineSegment(sketch, "E337", {"start": v(-16.82, -7) * mm, "end": v(-16.91, -7.7) * mm});
            skLineSegment(sketch, "E338", {"start": v(-16.91, -7.7) * mm, "end": v(-17, -8.39) * mm});
            skLineSegment(sketch, "E339", {"start": v(-17, -8.39) * mm, "end": v(-17.05, -9.08) * mm});
            skLineSegment(sketch, "E340", {"start": v(-17.05, -9.08) * mm, "end": v(-17.1, -9.78) * mm});
            skLineSegment(sketch, "E341", {"start": v(-17.1, -9.78) * mm, "end": v(-17.11, -10.48) * mm});
            skLineSegment(sketch, "E342", {"start": v(-17.11, -10.48) * mm, "end": v(-17.11, -11.18) * mm});
            skLineSegment(sketch, "E343", {"start": v(-17.11, -11.18) * mm, "end": v(-17.1, -11.88) * mm});
            skLineSegment(sketch, "E344", {"start": v(-17.1, -11.88) * mm, "end": v(-17.06, -12.58) * mm});
            skLineSegment(sketch, "E345", {"start": v(-17.06, -12.58) * mm, "end": v(-17, -13.28) * mm});
            skLineSegment(sketch, "E346", {"start": v(-17, -13.28) * mm, "end": v(-16.92, -13.97) * mm});
            skLineSegment(sketch, "E347", {"start": v(-16.92, -13.97) * mm, "end": v(-16.82, -14.66) * mm});
            skLineSegment(sketch, "E348", {"start": v(-16.82, -14.66) * mm, "end": v(-16.7, -15.35) * mm});
            skLineSegment(sketch, "E349", {"start": v(-16.7, -15.35) * mm, "end": v(-16.56, -16.03) * mm});
            skLineSegment(sketch, "E350", {"start": v(-16.56, -16.03) * mm, "end": v(-16.4, -16.7) * mm});
            skLineSegment(sketch, "E351", {"start": v(-16.4, -16.7) * mm, "end": v(-16.22, -17.36) * mm});
            skLineSegment(sketch, "E352", {"start": v(-16.22, -17.36) * mm, "end": v(-16.01, -18.02) * mm});
            skLineSegment(sketch, "E353", {"start": v(-16.01, -18.02) * mm, "end": v(-12.8, -25.36) * mm});
            skLineSegment(sketch, "E354", {"start": v(-12.8, -25.36) * mm, "end": v(-7.97, -30.87) * mm});
            skLineSegment(sketch, "E355", {"start": v(-7.97, -30.87) * mm, "end": v(-7.17, -30.87) * mm});
            skLineSegment(sketch, "E356", {"start": v(-7.17, -30.87) * mm, "end": v(-6.5, -27.16) * mm});
            skLineSegment(sketch, "E357", {"start": v(-6.5, -27.16) * mm, "end": v(-6.14, -25.32) * mm});
            skLineSegment(sketch, "E358", {"start": v(-6.14, -25.32) * mm, "end": v(-5.76, -23.48) * mm});
            skLineSegment(sketch, "E359", {"start": v(-5.76, -23.48) * mm, "end": v(-5.36, -21.64) * mm});
            skLineSegment(sketch, "E360", {"start": v(-5.36, -21.64) * mm, "end": v(-4.92, -19.81) * mm});
            skLineSegment(sketch, "E361", {"start": v(-4.92, -19.81) * mm, "end": v(-4.46, -18) * mm});
            skLineSegment(sketch, "E362", {"start": v(-4.46, -18) * mm, "end": v(-3.95, -16.18) * mm});
            skLineSegment(sketch, "E363", {"start": v(-3.95, -16.18) * mm, "end": v(2.48, -3.33) * mm});
            skLineSegment(sketch, "E364", {"start": v(2.48, -3.33) * mm, "end": v(3.93, -1.52) * mm});
            skLineSegment(sketch, "E365", {"start": v(3.93, -1.52) * mm, "end": v(5.4, 0.27) * mm});
            skLineSegment(sketch, "E366", {"start": v(81.28, 29.7) * mm, "end": v(81.28, 26.04) * mm});
            skLineSegment(sketch, "E367", {"start": v(81.28, 26.04) * mm, "end": v(84.5, 10.43) * mm});
            skLineSegment(sketch, "E368", {"start": v(84.5, 10.43) * mm, "end": v(85.14, 8.3) * mm});
            skLineSegment(sketch, "E369", {"start": v(85.14, 8.3) * mm, "end": v(85.48, 7.24) * mm});
            skLineSegment(sketch, "E370", {"start": v(85.48, 7.24) * mm, "end": v(85.85, 6.2) * mm});
            skLineSegment(sketch, "E371", {"start": v(85.85, 6.2) * mm, "end": v(86.25, 5.16) * mm});
            skLineSegment(sketch, "E372", {"start": v(86.25, 5.16) * mm, "end": v(86.7, 4.14) * mm});
            skLineSegment(sketch, "E373", {"start": v(86.7, 4.14) * mm, "end": v(87.18, 3.15) * mm});
            skLineSegment(sketch, "E374", {"start": v(87.18, 3.15) * mm, "end": v(87.44, 2.66) * mm});
            skLineSegment(sketch, "E375", {"start": v(87.44, 2.66) * mm, "end": v(87.71, 2.17) * mm});
            skLineSegment(sketch, "E376", {"start": v(87.71, 2.17) * mm, "end": v(88.3, 1.2) * mm});
            skLineSegment(sketch, "E377", {"start": v(88.3, 1.2) * mm, "end": v(88.92, 0.22) * mm});
            skLineSegment(sketch, "E378", {"start": v(88.92, 0.22) * mm, "end": v(89.52, -0.77) * mm});
            skLineSegment(sketch, "E379", {"start": v(89.52, -0.77) * mm, "end": v(90.1, -1.76) * mm});
            skLineSegment(sketch, "E380", {"start": v(90.1, -1.76) * mm, "end": v(90.38, -2.27) * mm});
            skLineSegment(sketch, "E381", {"start": v(90.38, -2.27) * mm, "end": v(90.64, -2.78) * mm});
            skLineSegment(sketch, "E382", {"start": v(90.64, -2.78) * mm, "end": v(90.88, -3.3) * mm});
            skLineSegment(sketch, "E383", {"start": v(90.88, -3.3) * mm, "end": v(91.1, -3.84) * mm});
            skLineSegment(sketch, "E384", {"start": v(91.1, -3.84) * mm, "end": v(91.3, -4.38) * mm});
            skLineSegment(sketch, "E385", {"start": v(91.3, -4.38) * mm, "end": v(91.48, -4.94) * mm});
            skLineSegment(sketch, "E386", {"start": v(91.48, -4.94) * mm, "end": v(91.62, -5.5) * mm});
            skLineSegment(sketch, "E387", {"start": v(91.62, -5.5) * mm, "end": v(91.73, -6.09) * mm});
            skLineSegment(sketch, "E388", {"start": v(91.73, -6.09) * mm, "end": v(91.82, -6.7) * mm});
            skLineSegment(sketch, "E389", {"start": v(91.82, -6.7) * mm, "end": v(91.89, -7.33) * mm});
            skLineSegment(sketch, "E390", {"start": v(91.89, -7.33) * mm, "end": v(91.94, -7.96) * mm});
            skLineSegment(sketch, "E391", {"start": v(91.94, -7.96) * mm, "end": v(91.97, -8.59) * mm});
            skLineSegment(sketch, "E392", {"start": v(91.97, -8.59) * mm, "end": v(92, -9.85) * mm});
            skLineSegment(sketch, "E393", {"start": v(92, -9.85) * mm, "end": v(91.98, -11.12) * mm});
            skLineSegment(sketch, "E394", {"start": v(91.98, -11.12) * mm, "end": v(91.93, -12.39) * mm});
            skLineSegment(sketch, "E395", {"start": v(91.93, -12.39) * mm, "end": v(91.86, -13.65) * mm});
            skLineSegment(sketch, "E396", {"start": v(91.86, -13.65) * mm, "end": v(91.8, -14.92) * mm});
            skLineSegment(sketch, "E397", {"start": v(91.8, -14.92) * mm, "end": v(91.73, -16.18) * mm});
            skLineSegment(sketch, "E398", {"start": v(91.73, -16.18) * mm, "end": v(90.93, -29.03) * mm});
            skLineSegment(sketch, "E399", {"start": v(90.93, -29.03) * mm, "end": v(91.16, -29.28) * mm});
            skLineSegment(sketch, "E400", {"start": v(91.16, -29.28) * mm, "end": v(91.42, -29.5) * mm});
            skLineSegment(sketch, "E401", {"start": v(91.42, -29.5) * mm, "end": v(91.7, -29.67) * mm});
            skLineSegment(sketch, "E402", {"start": v(91.7, -29.67) * mm, "end": v(92, -29.81) * mm});
            skLineSegment(sketch, "E403", {"start": v(92, -29.81) * mm, "end": v(92.31, -29.92) * mm});
            skLineSegment(sketch, "E404", {"start": v(92.31, -29.92) * mm, "end": v(92.64, -29.98) * mm});
            skLineSegment(sketch, "E405", {"start": v(92.64, -29.98) * mm, "end": v(92.98, -29.99) * mm});
            skLineSegment(sketch, "E406", {"start": v(92.98, -29.99) * mm, "end": v(93.34, -29.95) * mm});
            skLineSegment(sketch, "E407", {"start": v(93.34, -29.95) * mm, "end": v(94.81, -29.2) * mm});
            skLineSegment(sketch, "E408", {"start": v(94.81, -29.2) * mm, "end": v(96.28, -28.4) * mm});
            skLineSegment(sketch, "E409", {"start": v(96.28, -28.4) * mm, "end": v(97.73, -27.58) * mm});
            skLineSegment(sketch, "E410", {"start": v(97.73, -27.58) * mm, "end": v(99.16, -26.7) * mm});
            skLineSegment(sketch, "E411", {"start": v(99.16, -26.7) * mm, "end": v(99.86, -26.26) * mm});
            skLineSegment(sketch, "E412", {"start": v(99.86, -26.26) * mm, "end": v(100.56, -25.79) * mm});
            skLineSegment(sketch, "E413", {"start": v(100.56, -25.79) * mm, "end": v(101.25, -25.3) * mm});
            skLineSegment(sketch, "E414", {"start": v(101.25, -25.3) * mm, "end": v(101.94, -24.8) * mm});
            skLineSegment(sketch, "E415", {"start": v(101.94, -24.8) * mm, "end": v(102.62, -24.28) * mm});
            skLineSegment(sketch, "E416", {"start": v(102.62, -24.28) * mm, "end": v(103.28, -23.75) * mm});
            skLineSegment(sketch, "E417", {"start": v(103.28, -23.75) * mm, "end": v(103.94, -23.19) * mm});
            skLineSegment(sketch, "E418", {"start": v(103.94, -23.19) * mm, "end": v(104.6, -22.6) * mm});
            skLineSegment(sketch, "E419", {"start": v(104.6, -22.6) * mm, "end": v(105.4, -20.77) * mm});
            skLineSegment(sketch, "E420", {"start": v(105.4, -20.77) * mm, "end": v(105.42, -19.37) * mm});
            skLineSegment(sketch, "E421", {"start": v(105.42, -19.37) * mm, "end": v(105.45, -17.97) * mm});
            skLineSegment(sketch, "E422", {"start": v(105.45, -17.97) * mm, "end": v(105.48, -16.56) * mm});
            skLineSegment(sketch, "E423", {"start": v(105.48, -16.56) * mm, "end": v(105.47, -15.16) * mm});
            skLineSegment(sketch, "E424", {"start": v(105.47, -15.16) * mm, "end": v(105.44, -14.46) * mm});
            skLineSegment(sketch, "E425", {"start": v(105.44, -14.46) * mm, "end": v(105.4, -13.77) * mm});
            skLineSegment(sketch, "E426", {"start": v(105.4, -13.77) * mm, "end": v(105.34, -13.09) * mm});
            skLineSegment(sketch, "E427", {"start": v(105.34, -13.09) * mm, "end": v(105.25, -12.4) * mm});
            skLineSegment(sketch, "E428", {"start": v(105.25, -12.4) * mm, "end": v(105.14, -11.73) * mm});
            skLineSegment(sketch, "E429", {"start": v(105.14, -11.73) * mm, "end": v(105, -11.07) * mm});
            skLineSegment(sketch, "E430", {"start": v(105, -11.07) * mm, "end": v(104.81, -10.4) * mm});
            skLineSegment(sketch, "E431", {"start": v(104.81, -10.4) * mm, "end": v(104.6, -9.76) * mm});
            skLineSegment(sketch, "E432", {"start": v(104.6, -9.76) * mm, "end": v(97.36, 7.68) * mm});
            skLineSegment(sketch, "E433", {"start": v(97.36, 7.68) * mm, "end": v(97.1, 8.57) * mm});
            skLineSegment(sketch, "E434", {"start": v(97.1, 8.57) * mm, "end": v(96.9, 9.47) * mm});
            skLineSegment(sketch, "E435", {"start": v(96.9, 9.47) * mm, "end": v(96.7, 10.39) * mm});
            skLineSegment(sketch, "E436", {"start": v(96.7, 10.39) * mm, "end": v(96.57, 11.31) * mm});
            skLineSegment(sketch, "E437", {"start": v(96.57, 11.31) * mm, "end": v(96.48, 12.24) * mm});
            skLineSegment(sketch, "E438", {"start": v(96.48, 12.24) * mm, "end": v(96.44, 13.17) * mm});
            skLineSegment(sketch, "E439", {"start": v(96.44, 13.17) * mm, "end": v(96.45, 13.64) * mm});
            skLineSegment(sketch, "E440", {"start": v(96.45, 13.64) * mm, "end": v(96.47, 14.1) * mm});
            skLineSegment(sketch, "E441", {"start": v(96.47, 14.1) * mm, "end": v(96.5, 14.56) * mm});
            skLineSegment(sketch, "E442", {"start": v(96.5, 14.56) * mm, "end": v(96.55, 15.02) * mm});
            skLineSegment(sketch, "E443", {"start": v(96.55, 15.02) * mm, "end": v(98.16, 19.61) * mm});
            skLineSegment(sketch, "E444", {"start": v(98.16, 19.61) * mm, "end": v(98.16, 19.97) * mm});
            skLineSegment(sketch, "E445", {"start": v(98.16, 19.97) * mm, "end": v(98.14, 20.33) * mm});
            skLineSegment(sketch, "E446", {"start": v(98.14, 20.33) * mm, "end": v(98.1, 20.69) * mm});
            skLineSegment(sketch, "E447", {"start": v(98.1, 20.69) * mm, "end": v(98.03, 21.04) * mm});
            skLineSegment(sketch, "E448", {"start": v(98.03, 21.04) * mm, "end": v(97.93, 21.38) * mm});
            skLineSegment(sketch, "E449", {"start": v(97.93, 21.38) * mm, "end": v(97.8, 21.72) * mm});
            skLineSegment(sketch, "E450", {"start": v(97.8, 21.72) * mm, "end": v(97.6, 22.05) * mm});
            skLineSegment(sketch, "E451", {"start": v(97.6, 22.05) * mm, "end": v(97.36, 22.37) * mm});
            skLineSegment(sketch, "E452", {"start": v(97.36, 22.37) * mm, "end": v(92.53, 26.04) * mm});
            skLineSegment(sketch, "E453", {"start": v(92.53, 26.04) * mm, "end": v(82.89, 29.7) * mm});
            skLineSegment(sketch, "E454", {"start": v(82.89, 29.7) * mm, "end": v(81.28, 29.7) * mm});
            skLineSegment(sketch, "E455", {"start": v(-20.84, 22.37) * mm, "end": v(-31.29, 17.78) * mm});
            skLineSegment(sketch, "E456", {"start": v(-31.29, 17.78) * mm, "end": v(-31.29, 15.02) * mm});
            skLineSegment(sketch, "E457", {"start": v(-31.29, 15.02) * mm, "end": v(-29.68, 7.68) * mm});
            skLineSegment(sketch, "E458", {"start": v(-29.68, 7.68) * mm, "end": v(-29.53, 6.18) * mm});
            skLineSegment(sketch, "E459", {"start": v(-29.53, 6.18) * mm, "end": v(-29.43, 4.66) * mm});
            skLineSegment(sketch, "E460", {"start": v(-29.43, 4.66) * mm, "end": v(-29.37, 3.13) * mm});
            skLineSegment(sketch, "E461", {"start": v(-29.37, 3.13) * mm, "end": v(-29.35, 1.6) * mm});
            skLineSegment(sketch, "E462", {"start": v(-29.35, 1.6) * mm, "end": v(-29.33, -1.48) * mm});
            skLineSegment(sketch, "E463", {"start": v(-29.33, -1.48) * mm, "end": v(-29.32, -3.01) * mm});
            skLineSegment(sketch, "E464", {"start": v(-29.32, -3.01) * mm, "end": v(-29.3, -4.54) * mm});
            skLineSegment(sketch, "E465", {"start": v(-29.3, -4.54) * mm, "end": v(-29.25, -6.06) * mm});
            skLineSegment(sketch, "E466", {"start": v(-29.25, -6.06) * mm, "end": v(-29.17, -7.57) * mm});
            skLineSegment(sketch, "E467", {"start": v(-29.17, -7.57) * mm, "end": v(-29.03, -9.06) * mm});
            skLineSegment(sketch, "E468", {"start": v(-29.03, -9.06) * mm, "end": v(-28.95, -9.8) * mm});
            skLineSegment(sketch, "E469", {"start": v(-28.95, -9.8) * mm, "end": v(-28.84, -10.54) * mm});
            skLineSegment(sketch, "E470", {"start": v(-28.84, -10.54) * mm, "end": v(-28.72, -11.27) * mm});
            skLineSegment(sketch, "E471", {"start": v(-28.72, -11.27) * mm, "end": v(-28.58, -11.99) * mm});
            skLineSegment(sketch, "E472", {"start": v(-28.58, -11.99) * mm, "end": v(-28.42, -12.7) * mm});
            skLineSegment(sketch, "E473", {"start": v(-28.42, -12.7) * mm, "end": v(-28.24, -13.42) * mm});
            skLineSegment(sketch, "E474", {"start": v(-28.24, -13.42) * mm, "end": v(-28.03, -14.12) * mm});
            skLineSegment(sketch, "E475", {"start": v(-28.03, -14.12) * mm, "end": v(-27.8, -14.82) * mm});
            skLineSegment(sketch, "E476", {"start": v(-27.8, -14.82) * mm, "end": v(-27.55, -15.5) * mm});
            skLineSegment(sketch, "E477", {"start": v(-27.55, -15.5) * mm, "end": v(-27.27, -16.18) * mm});
            skLineSegment(sketch, "E478", {"start": v(-27.27, -16.18) * mm, "end": v(-26.94, -16.92) * mm});
            skLineSegment(sketch, "E479", {"start": v(-26.94, -16.92) * mm, "end": v(-26.6, -17.65) * mm});
            skLineSegment(sketch, "E480", {"start": v(-26.6, -17.65) * mm, "end": v(-26.24, -18.37) * mm});
            skLineSegment(sketch, "E481", {"start": v(-26.24, -18.37) * mm, "end": v(-25.86, -19.07) * mm});
            skLineSegment(sketch, "E482", {"start": v(-25.86, -19.07) * mm, "end": v(-25.46, -19.76) * mm});
            skLineSegment(sketch, "E483", {"start": v(-25.46, -19.76) * mm, "end": v(-25.03, -20.43) * mm});
            skLineSegment(sketch, "E484", {"start": v(-25.03, -20.43) * mm, "end": v(-24.56, -21.07) * mm});
            skLineSegment(sketch, "E485", {"start": v(-24.56, -21.07) * mm, "end": v(-24.05, -21.7) * mm});
            skLineSegment(sketch, "E486", {"start": v(-24.05, -21.7) * mm, "end": v(-20.03, -23.53) * mm});
            skLineSegment(sketch, "E487", {"start": v(-20.03, -23.53) * mm, "end": v(-18.42, -22.6) * mm});
            skLineSegment(sketch, "E488", {"start": v(-18.42, -22.6) * mm, "end": v(-18.98, -18.26) * mm});
            skLineSegment(sketch, "E489", {"start": v(-18.98, -18.26) * mm, "end": v(-19.24, -16.07) * mm});
            skLineSegment(sketch, "E490", {"start": v(-19.24, -16.07) * mm, "end": v(-19.35, -14.97) * mm});
            skLineSegment(sketch, "E491", {"start": v(-19.35, -14.97) * mm, "end": v(-19.44, -13.88) * mm});
            skLineSegment(sketch, "E492", {"start": v(-19.44, -13.88) * mm, "end": v(-19.52, -12.78) * mm});
            skLineSegment(sketch, "E493", {"start": v(-19.52, -12.78) * mm, "end": v(-19.57, -11.69) * mm});
            skLineSegment(sketch, "E494", {"start": v(-19.57, -11.69) * mm, "end": v(-19.6, -10.6) * mm});
            skLineSegment(sketch, "E495", {"start": v(-19.6, -10.6) * mm, "end": v(-19.6, -9.5) * mm});
            skLineSegment(sketch, "E496", {"start": v(-19.6, -9.5) * mm, "end": v(-19.56, -8.42) * mm});
            skLineSegment(sketch, "E497", {"start": v(-19.56, -8.42) * mm, "end": v(-19.49, -7.33) * mm});
            skLineSegment(sketch, "E498", {"start": v(-19.49, -7.33) * mm, "end": v(-19.38, -6.25) * mm});
            skLineSegment(sketch, "E499", {"start": v(-19.38, -6.25) * mm, "end": v(-19.23, -5.17) * mm});
            skLineSegment(sketch, "E500", {"start": v(-19.23, -5.17) * mm, "end": v(-19.08, -4.45) * mm});
            skLineSegment(sketch, "E501", {"start": v(-19.08, -4.45) * mm, "end": v(-18.9, -3.74) * mm});
            skLineSegment(sketch, "E502", {"start": v(-18.9, -3.74) * mm, "end": v(-18.66, -3.06) * mm});
            skLineSegment(sketch, "E503", {"start": v(-18.66, -3.06) * mm, "end": v(-18.4, -2.39) * mm});
            skLineSegment(sketch, "E504", {"start": v(-18.4, -2.39) * mm, "end": v(-18.09, -1.73) * mm});
            skLineSegment(sketch, "E505", {"start": v(-18.09, -1.73) * mm, "end": v(-17.75, -1.1) * mm});
            skLineSegment(sketch, "E506", {"start": v(-17.75, -1.1) * mm, "end": v(-17.4, -0.46) * mm});
            skLineSegment(sketch, "E507", {"start": v(-17.4, -0.46) * mm, "end": v(-17, 0.16) * mm});
            skLineSegment(sketch, "E508", {"start": v(-17, 0.16) * mm, "end": v(-16.6, 0.77) * mm});
            skLineSegment(sketch, "E509", {"start": v(-16.6, 0.77) * mm, "end": v(-16.19, 1.37) * mm});
            skLineSegment(sketch, "E510", {"start": v(-16.19, 1.37) * mm, "end": v(-15.32, 2.56) * mm});
            skLineSegment(sketch, "E511", {"start": v(-15.32, 2.56) * mm, "end": v(-14.45, 3.75) * mm});
            skLineSegment(sketch, "E512", {"start": v(-14.45, 3.75) * mm, "end": v(-13.6, 4.93) * mm});
            skLineSegment(sketch, "E513", {"start": v(-13.6, 4.93) * mm, "end": v(-10.38, 8.6) * mm});
            skLineSegment(sketch, "E514", {"start": v(-10.38, 8.6) * mm, "end": v(-9.89, 9.2) * mm});
            skLineSegment(sketch, "E515", {"start": v(-9.89, 9.2) * mm, "end": v(-9.43, 9.83) * mm});
            skLineSegment(sketch, "E516", {"start": v(-9.43, 9.83) * mm, "end": v(-9, 10.5) * mm});
            skLineSegment(sketch, "E517", {"start": v(-9, 10.5) * mm, "end": v(-8.6, 11.18) * mm});
            skLineSegment(sketch, "E518", {"start": v(-8.6, 11.18) * mm, "end": v(-8.21, 11.89) * mm});
            skLineSegment(sketch, "E519", {"start": v(-8.21, 11.89) * mm, "end": v(-7.85, 12.61) * mm});
            skLineSegment(sketch, "E520", {"start": v(-7.85, 12.61) * mm, "end": v(-7.5, 13.35) * mm});
            skLineSegment(sketch, "E521", {"start": v(-7.5, 13.35) * mm, "end": v(-7.17, 14.1) * mm});
            skLineSegment(sketch, "E522", {"start": v(-7.17, 14.1) * mm, "end": v(-7.19, 14.72) * mm});
            skLineSegment(sketch, "E523", {"start": v(-7.19, 14.72) * mm, "end": v(-7.25, 15.32) * mm});
            skLineSegment(sketch, "E524", {"start": v(-7.25, 15.32) * mm, "end": v(-7.36, 15.92) * mm});
            skLineSegment(sketch, "E525", {"start": v(-7.36, 15.92) * mm, "end": v(-7.52, 16.5) * mm});
            skLineSegment(sketch, "E526", {"start": v(-7.52, 16.5) * mm, "end": v(-7.62, 16.79) * mm});
            skLineSegment(sketch, "E527", {"start": v(-7.62, 16.79) * mm, "end": v(-7.73, 17.07) * mm});
            skLineSegment(sketch, "E528", {"start": v(-7.73, 17.07) * mm, "end": v(-7.87, 17.35) * mm});
            skLineSegment(sketch, "E529", {"start": v(-7.87, 17.35) * mm, "end": v(-8.01, 17.63) * mm});
            skLineSegment(sketch, "E530", {"start": v(-8.01, 17.63) * mm, "end": v(-8.18, 17.9) * mm});
            skLineSegment(sketch, "E531", {"start": v(-8.18, 17.9) * mm, "end": v(-8.36, 18.17) * mm});
            skLineSegment(sketch, "E532", {"start": v(-8.36, 18.17) * mm, "end": v(-8.56, 18.43) * mm});
            skLineSegment(sketch, "E533", {"start": v(-8.56, 18.43) * mm, "end": v(-8.77, 18.7) * mm});
            skLineSegment(sketch, "E534", {"start": v(-8.77, 18.7) * mm, "end": v(-15.2, 22.37) * mm});
            skLineSegment(sketch, "E535", {"start": v(-15.2, 22.37) * mm, "end": v(-20.84, 22.37) * mm});
            skLineSegment(sketch, "E536", {"start": v(61.18, -2.42) * mm, "end": v(63.59, -7) * mm});
            skLineSegment(sketch, "E537", {"start": v(63.59, -7) * mm, "end": v(63.6, -8.38) * mm});
            skLineSegment(sketch, "E538", {"start": v(63.6, -8.38) * mm, "end": v(63.64, -9.76) * mm});
            skLineSegment(sketch, "E539", {"start": v(63.64, -9.76) * mm, "end": v(63.72, -12.52) * mm});
            skLineSegment(sketch, "E540", {"start": v(63.72, -12.52) * mm, "end": v(63.74, -13.9) * mm});
            skLineSegment(sketch, "E541", {"start": v(63.74, -13.9) * mm, "end": v(63.73, -15.28) * mm});
            skLineSegment(sketch, "E542", {"start": v(63.73, -15.28) * mm, "end": v(63.69, -16.65) * mm});
            skLineSegment(sketch, "E543", {"start": v(63.69, -16.65) * mm, "end": v(63.65, -17.34) * mm});
            skLineSegment(sketch, "E544", {"start": v(63.65, -17.34) * mm, "end": v(63.59, -18.02) * mm});
            skLineSegment(sketch, "E545", {"start": v(63.59, -18.02) * mm, "end": v(62.79, -23.53) * mm});
            skLineSegment(sketch, "E546", {"start": v(62.79, -23.53) * mm, "end": v(63.11, -23.88) * mm});
            skLineSegment(sketch, "E547", {"start": v(63.11, -23.88) * mm, "end": v(63.29, -24.03) * mm});
            skLineSegment(sketch, "E548", {"start": v(63.29, -24.03) * mm, "end": v(63.47, -24.17) * mm});
            skLineSegment(sketch, "E549", {"start": v(63.47, -24.17) * mm, "end": v(63.68, -24.28) * mm});
            skLineSegment(sketch, "E550", {"start": v(63.68, -24.28) * mm, "end": v(63.9, -24.37) * mm});
            skLineSegment(sketch, "E551", {"start": v(63.9, -24.37) * mm, "end": v(64.13, -24.43) * mm});
            skLineSegment(sketch, "E552", {"start": v(64.13, -24.43) * mm, "end": v(64.4, -24.45) * mm});
            skLineSegment(sketch, "E553", {"start": v(64.4, -24.45) * mm, "end": v(65.2, -23.03) * mm});
            skLineSegment(sketch, "E554", {"start": v(65.2, -23.03) * mm, "end": v(65.98, -21.58) * mm});
            skLineSegment(sketch, "E555", {"start": v(65.98, -21.58) * mm, "end": v(66.72, -20.12) * mm});
            skLineSegment(sketch, "E556", {"start": v(66.72, -20.12) * mm, "end": v(67.44, -18.64) * mm});
            skLineSegment(sketch, "E557", {"start": v(67.44, -18.64) * mm, "end": v(68.13, -17.14) * mm});
            skLineSegment(sketch, "E558", {"start": v(68.13, -17.14) * mm, "end": v(68.79, -15.61) * mm});
            skLineSegment(sketch, "E559", {"start": v(68.79, -15.61) * mm, "end": v(69.42, -14.07) * mm});
            skLineSegment(sketch, "E560", {"start": v(69.42, -14.07) * mm, "end": v(70.02, -12.51) * mm});
            skLineSegment(sketch, "E561", {"start": v(70.02, -12.51) * mm, "end": v(70.12, -11.83) * mm});
            skLineSegment(sketch, "E562", {"start": v(70.12, -11.83) * mm, "end": v(70.19, -11.15) * mm});
            skLineSegment(sketch, "E563", {"start": v(70.19, -11.15) * mm, "end": v(70.24, -10.47) * mm});
            skLineSegment(sketch, "E564", {"start": v(70.24, -10.47) * mm, "end": v(70.27, -9.79) * mm});
            skLineSegment(sketch, "E565", {"start": v(70.27, -9.79) * mm, "end": v(70.28, -9.1) * mm});
            skLineSegment(sketch, "E566", {"start": v(70.28, -9.1) * mm, "end": v(70.28, -8.4) * mm});
            skLineSegment(sketch, "E567", {"start": v(70.28, -8.4) * mm, "end": v(70.24, -7.03) * mm});
            skLineSegment(sketch, "E568", {"start": v(70.24, -7.03) * mm, "end": v(70.1, -4.26) * mm});
            skLineSegment(sketch, "E569", {"start": v(70.1, -4.26) * mm, "end": v(70.05, -2.88) * mm});
            skLineSegment(sketch, "E570", {"start": v(70.05, -2.88) * mm, "end": v(70.02, -1.5) * mm});
            skLineSegment(sketch, "E571", {"start": v(70.02, -1.5) * mm, "end": v(63.83, 9.92) * mm});
            skLineSegment(sketch, "E572", {"start": v(12.1, -10.82) * mm, "end": v(12.12, -11.42) * mm});
            skLineSegment(sketch, "E573", {"start": v(12.12, -11.42) * mm, "end": v(12.15, -12.01) * mm});
            skLineSegment(sketch, "E574", {"start": v(12.15, -12.01) * mm, "end": v(12.2, -12.6) * mm});
            skLineSegment(sketch, "E575", {"start": v(12.2, -12.6) * mm, "end": v(12.27, -13.2) * mm});
            skLineSegment(sketch, "E576", {"start": v(12.27, -13.2) * mm, "end": v(12.35, -13.78) * mm});
            skLineSegment(sketch, "E577", {"start": v(12.35, -13.78) * mm, "end": v(12.46, -14.36) * mm});
            skLineSegment(sketch, "E578", {"start": v(12.46, -14.36) * mm, "end": v(12.59, -14.94) * mm});
            skLineSegment(sketch, "E579", {"start": v(12.59, -14.94) * mm, "end": v(12.73, -15.51) * mm});
            skLineSegment(sketch, "E580", {"start": v(12.73, -15.51) * mm, "end": v(12.9, -16.08) * mm});
            skLineSegment(sketch, "E581", {"start": v(12.9, -16.08) * mm, "end": v(13.08, -16.64) * mm});
            skLineSegment(sketch, "E582", {"start": v(13.08, -16.64) * mm, "end": v(13.27, -17.2) * mm});
            skLineSegment(sketch, "E583", {"start": v(13.27, -17.2) * mm, "end": v(13.5, -17.74) * mm});
            skLineSegment(sketch, "E584", {"start": v(13.5, -17.74) * mm, "end": v(13.73, -18.28) * mm});
            skLineSegment(sketch, "E585", {"start": v(13.73, -18.28) * mm, "end": v(13.98, -18.82) * mm});
            skLineSegment(sketch, "E586", {"start": v(13.98, -18.82) * mm, "end": v(14.25, -19.34) * mm});
            skLineSegment(sketch, "E587", {"start": v(14.25, -19.34) * mm, "end": v(14.54, -19.86) * mm});
            skLineSegment(sketch, "E588", {"start": v(14.54, -19.86) * mm, "end": v(15.28, -20.55) * mm});
            skLineSegment(sketch, "E589", {"start": v(15.28, -20.55) * mm, "end": v(16.02, -21.27) * mm});
            skLineSegment(sketch, "E590", {"start": v(16.02, -21.27) * mm, "end": v(16.77, -21.98) * mm});
            skLineSegment(sketch, "E591", {"start": v(16.77, -21.98) * mm, "end": v(17.54, -22.65) * mm});
            skLineSegment(sketch, "E592", {"start": v(17.54, -22.65) * mm, "end": v(17.93, -22.96) * mm});
            skLineSegment(sketch, "E593", {"start": v(17.93, -22.96) * mm, "end": v(18.33, -23.26) * mm});
            skLineSegment(sketch, "E594", {"start": v(18.33, -23.26) * mm, "end": v(18.74, -23.53) * mm});
            skLineSegment(sketch, "E595", {"start": v(18.74, -23.53) * mm, "end": v(19.16, -23.78) * mm});
            skLineSegment(sketch, "E596", {"start": v(19.16, -23.78) * mm, "end": v(19.6, -24) * mm});
            skLineSegment(sketch, "E597", {"start": v(19.6, -24) * mm, "end": v(20.04, -24.18) * mm});
            skLineSegment(sketch, "E598", {"start": v(20.04, -24.18) * mm, "end": v(20.5, -24.33) * mm});
            skLineSegment(sketch, "E599", {"start": v(20.5, -24.33) * mm, "end": v(20.97, -24.45) * mm});
            skLineSegment(sketch, "E600", {"start": v(20.97, -24.45) * mm, "end": v(24.2, -24.45) * mm});
            skLineSegment(sketch, "E601", {"start": v(24.2, -24.45) * mm, "end": v(24.45, -21.58) * mm});
            skLineSegment(sketch, "E602", {"start": v(24.45, -21.58) * mm, "end": v(24.59, -20.15) * mm});
            skLineSegment(sketch, "E603", {"start": v(24.59, -20.15) * mm, "end": v(24.74, -18.72) * mm});
            skLineSegment(sketch, "E604", {"start": v(27.58, -19.48) * mm, "end": v(27.67, -20.58) * mm});
            skLineSegment(sketch, "E605", {"start": v(27.67, -20.58) * mm, "end": v(27.78, -21.67) * mm});
            skLineSegment(sketch, "E606", {"start": v(27.78, -21.67) * mm, "end": v(27.9, -22.76) * mm});
            skLineSegment(sketch, "E607", {"start": v(27.9, -22.76) * mm, "end": v(28.07, -23.85) * mm});
            skLineSegment(sketch, "E608", {"start": v(28.07, -23.85) * mm, "end": v(28.26, -24.93) * mm});
            skLineSegment(sketch, "E609", {"start": v(28.26, -24.93) * mm, "end": v(28.47, -26) * mm});
            skLineSegment(sketch, "E610", {"start": v(28.47, -26) * mm, "end": v(28.73, -27.06) * mm});
            skLineSegment(sketch, "E611", {"start": v(28.73, -27.06) * mm, "end": v(29.02, -28.12) * mm});
            skLineSegment(sketch, "E612", {"start": v(29.02, -28.12) * mm, "end": v(30.62, -30.87) * mm});
            skLineSegment(sketch, "E613", {"start": v(30.62, -30.87) * mm, "end": v(37.86, -33.62) * mm});
            skLineSegment(sketch, "E614", {"start": v(37.86, -33.62) * mm, "end": v(37.85, -33.27) * mm});
            skLineSegment(sketch, "E615", {"start": v(37.85, -33.27) * mm, "end": v(37.82, -32.92) * mm});
            skLineSegment(sketch, "E616", {"start": v(37.82, -32.92) * mm, "end": v(37.77, -32.58) * mm});
            skLineSegment(sketch, "E617", {"start": v(37.77, -32.58) * mm, "end": v(37.69, -32.24) * mm});
            skLineSegment(sketch, "E618", {"start": v(37.69, -32.24) * mm, "end": v(37.58, -31.9) * mm});
            skLineSegment(sketch, "E619", {"start": v(37.58, -31.9) * mm, "end": v(37.44, -31.57) * mm});
            skLineSegment(sketch, "E620", {"start": v(37.44, -31.57) * mm, "end": v(37.27, -31.22) * mm});
            skLineSegment(sketch, "E621", {"start": v(37.27, -31.22) * mm, "end": v(37.06, -30.87) * mm});
            skLineSegment(sketch, "E622", {"start": v(37.06, -30.87) * mm, "end": v(35.45, -27.2) * mm});
            skLineSegment(sketch, "E623", {"start": v(35.45, -27.2) * mm, "end": v(35.45, -20.09) * mm});
            skLineSegment(sketch, "E624", {"start": v(51.56, -14.33) * mm, "end": v(51.75, -14.99) * mm});
            skLineSegment(sketch, "E625", {"start": v(51.75, -14.99) * mm, "end": v(51.9, -15.66) * mm});
            skLineSegment(sketch, "E626", {"start": v(51.9, -15.66) * mm, "end": v(52.02, -16.35) * mm});
            skLineSegment(sketch, "E627", {"start": v(52.02, -16.35) * mm, "end": v(52.1, -17.05) * mm});
            skLineSegment(sketch, "E628", {"start": v(52.1, -17.05) * mm, "end": v(52.18, -17.75) * mm});
            skLineSegment(sketch, "E629", {"start": v(52.18, -17.75) * mm, "end": v(52.24, -18.46) * mm});
            skLineSegment(sketch, "E630", {"start": v(52.24, -18.46) * mm, "end": v(52.33, -19.86) * mm});
            skLineSegment(sketch, "E631", {"start": v(52.33, -19.86) * mm, "end": v(52.38, -20.84) * mm});
            skLineSegment(sketch, "E632", {"start": v(52.38, -20.84) * mm, "end": v(52.4, -21.84) * mm});
            skLineSegment(sketch, "E633", {"start": v(52.4, -21.84) * mm, "end": v(52.38, -22.83) * mm});
            skLineSegment(sketch, "E634", {"start": v(52.38, -22.83) * mm, "end": v(52.32, -23.82) * mm});
            skLineSegment(sketch, "E635", {"start": v(52.32, -23.82) * mm, "end": v(52.23, -24.81) * mm});
            skLineSegment(sketch, "E636", {"start": v(52.23, -24.81) * mm, "end": v(52.1, -25.8) * mm});
            skLineSegment(sketch, "E637", {"start": v(52.1, -25.8) * mm, "end": v(51.93, -26.76) * mm});
            skLineSegment(sketch, "E638", {"start": v(51.93, -26.76) * mm, "end": v(51.72, -27.72) * mm});
            skLineSegment(sketch, "E639", {"start": v(51.72, -27.72) * mm, "end": v(51.47, -28.66) * mm});
            skLineSegment(sketch, "E640", {"start": v(51.47, -28.66) * mm, "end": v(51.16, -29.58) * mm});
            skLineSegment(sketch, "E641", {"start": v(51.16, -29.58) * mm, "end": v(50.82, -30.48) * mm});
            skLineSegment(sketch, "E642", {"start": v(50.82, -30.48) * mm, "end": v(50.42, -31.35) * mm});
            skLineSegment(sketch, "E643", {"start": v(50.42, -31.35) * mm, "end": v(49.97, -32.2) * mm});
            skLineSegment(sketch, "E644", {"start": v(49.97, -32.2) * mm, "end": v(49.73, -32.61) * mm});
            skLineSegment(sketch, "E645", {"start": v(49.73, -32.61) * mm, "end": v(49.47, -33.01) * mm});
            skLineSegment(sketch, "E646", {"start": v(49.47, -33.01) * mm, "end": v(49.2, -33.4) * mm});
            skLineSegment(sketch, "E647", {"start": v(49.2, -33.4) * mm, "end": v(48.92, -33.8) * mm});
            skLineSegment(sketch, "E648", {"start": v(48.92, -33.8) * mm, "end": v(48.62, -34.17) * mm});
            skLineSegment(sketch, "E649", {"start": v(48.62, -34.17) * mm, "end": v(48.31, -34.54) * mm});
            skLineSegment(sketch, "E650", {"start": v(48.31, -34.54) * mm, "end": v(43.49, -36.38) * mm});
            skLineSegment(sketch, "E651", {"start": v(43.49, -36.38) * mm, "end": v(42.67, -36.47) * mm});
            skLineSegment(sketch, "E652", {"start": v(42.67, -36.47) * mm, "end": v(41.85, -36.5) * mm});
            skLineSegment(sketch, "E653", {"start": v(41.85, -36.5) * mm, "end": v(41.04, -36.5) * mm});
            skLineSegment(sketch, "E654", {"start": v(41.04, -36.5) * mm, "end": v(40.23, -36.44) * mm});
            skLineSegment(sketch, "E655", {"start": v(40.23, -36.44) * mm, "end": v(39.41, -36.34) * mm});
            skLineSegment(sketch, "E656", {"start": v(39.41, -36.34) * mm, "end": v(38.6, -36.2) * mm});
            skLineSegment(sketch, "E657", {"start": v(38.6, -36.2) * mm, "end": v(37.8, -36.03) * mm});
            skLineSegment(sketch, "E658", {"start": v(37.8, -36.03) * mm, "end": v(36.99, -35.83) * mm});
            skLineSegment(sketch, "E659", {"start": v(36.99, -35.83) * mm, "end": v(36.18, -35.6) * mm});
            skLineSegment(sketch, "E660", {"start": v(36.18, -35.6) * mm, "end": v(35.38, -35.36) * mm});
            skLineSegment(sketch, "E661", {"start": v(35.38, -35.36) * mm, "end": v(34.58, -35.1) * mm});
            skLineSegment(sketch, "E662", {"start": v(34.58, -35.1) * mm, "end": v(33.79, -34.81) * mm});
            skLineSegment(sketch, "E663", {"start": v(33.79, -34.81) * mm, "end": v(32.2, -34.23) * mm});
            skLineSegment(sketch, "E664", {"start": v(32.2, -34.23) * mm, "end": v(30.62, -33.62) * mm});
            skLineSegment(sketch, "E665", {"start": v(30.62, -33.62) * mm, "end": v(28.65, -32.61) * mm});
            skLineSegment(sketch, "E666", {"start": v(28.65, -32.61) * mm, "end": v(26.7, -31.58) * mm});
            skLineSegment(sketch, "E667", {"start": v(26.7, -31.58) * mm, "end": v(24.75, -30.51) * mm});
            skLineSegment(sketch, "E668", {"start": v(24.75, -30.51) * mm, "end": v(22.82, -29.4) * mm});
            skLineSegment(sketch, "E669", {"start": v(22.82, -29.4) * mm, "end": v(20.9, -28.26) * mm});
            skLineSegment(sketch, "E670", {"start": v(20.9, -28.26) * mm, "end": v(19.96, -27.66) * mm});
            skLineSegment(sketch, "E671", {"start": v(19.96, -27.66) * mm, "end": v(19.02, -27.05) * mm});
            skLineSegment(sketch, "E672", {"start": v(19.02, -27.05) * mm, "end": v(18.1, -26.42) * mm});
            skLineSegment(sketch, "E673", {"start": v(18.1, -26.42) * mm, "end": v(17.17, -25.78) * mm});
            skLineSegment(sketch, "E674", {"start": v(17.17, -25.78) * mm, "end": v(16.25, -25.12) * mm});
            skLineSegment(sketch, "E675", {"start": v(16.25, -25.12) * mm, "end": v(15.35, -24.45) * mm});
            skLineSegment(sketch, "E676", {"start": v(15.35, -24.45) * mm, "end": v(14.54, -24.45) * mm});
            skLineSegment(sketch, "E677", {"start": v(14.54, -24.45) * mm, "end": v(14.54, -26.77) * mm});
            skLineSegment(sketch, "E678", {"start": v(14.54, -26.77) * mm, "end": v(14.56, -27.94) * mm});
            skLineSegment(sketch, "E679", {"start": v(14.56, -27.94) * mm, "end": v(14.6, -29.1) * mm});
            skLineSegment(sketch, "E680", {"start": v(14.6, -29.1) * mm, "end": v(14.7, -30.26) * mm});
            skLineSegment(sketch, "E681", {"start": v(14.7, -30.26) * mm, "end": v(14.76, -30.83) * mm});
            skLineSegment(sketch, "E682", {"start": v(14.76, -30.83) * mm, "end": v(14.84, -31.4) * mm});
            skLineSegment(sketch, "E683", {"start": v(14.84, -31.4) * mm, "end": v(14.94, -31.96) * mm});
            skLineSegment(sketch, "E684", {"start": v(14.94, -31.96) * mm, "end": v(15.05, -32.52) * mm});
            skLineSegment(sketch, "E685", {"start": v(15.05, -32.52) * mm, "end": v(15.19, -33.08) * mm});
            skLineSegment(sketch, "E686", {"start": v(15.19, -33.08) * mm, "end": v(15.35, -33.62) * mm});
            skLineSegment(sketch, "E687", {"start": v(15.35, -33.62) * mm, "end": v(15.71, -34.42) * mm});
            skLineSegment(sketch, "E688", {"start": v(15.71, -34.42) * mm, "end": v(16.1, -35.19) * mm});
            skLineSegment(sketch, "E689", {"start": v(16.1, -35.19) * mm, "end": v(16.53, -35.93) * mm});
            skLineSegment(sketch, "E690", {"start": v(16.53, -35.93) * mm, "end": v(17, -36.64) * mm});
            skLineSegment(sketch, "E691", {"start": v(17, -36.64) * mm, "end": v(17.51, -37.32) * mm});
            skLineSegment(sketch, "E692", {"start": v(17.51, -37.32) * mm, "end": v(17.79, -37.65) * mm});
            skLineSegment(sketch, "E693", {"start": v(17.79, -37.65) * mm, "end": v(18.08, -37.97) * mm});
            skLineSegment(sketch, "E694", {"start": v(18.08, -37.97) * mm, "end": v(18.38, -38.27) * mm});
            skLineSegment(sketch, "E695", {"start": v(18.38, -38.27) * mm, "end": v(18.7, -38.57) * mm});
            skLineSegment(sketch, "E696", {"start": v(18.7, -38.57) * mm, "end": v(19.02, -38.86) * mm});
            skLineSegment(sketch, "E697", {"start": v(19.02, -38.86) * mm, "end": v(19.37, -39.13) * mm});
            skLineSegment(sketch, "E698", {"start": v(19.37, -39.13) * mm, "end": v(29.02, -46.47) * mm});
            skLineSegment(sketch, "E699", {"start": v(29.02, -46.47) * mm, "end": v(30.05, -47.4) * mm});
            skLineSegment(sketch, "E700", {"start": v(30.05, -47.4) * mm, "end": v(31.1, -48.28) * mm});
            skLineSegment(sketch, "E701", {"start": v(31.1, -48.28) * mm, "end": v(32.18, -49.13) * mm});
            skLineSegment(sketch, "E702", {"start": v(32.18, -49.13) * mm, "end": v(33.28, -49.95) * mm});
            skLineSegment(sketch, "E703", {"start": v(33.28, -49.95) * mm, "end": v(34.4, -50.73) * mm});
            skLineSegment(sketch, "E704", {"start": v(34.4, -50.73) * mm, "end": v(35.53, -51.49) * mm});
            skLineSegment(sketch, "E705", {"start": v(35.53, -51.49) * mm, "end": v(36.68, -52.2) * mm});
            skLineSegment(sketch, "E706", {"start": v(36.68, -52.2) * mm, "end": v(37.86, -52.9) * mm});
            skLineSegment(sketch, "E707", {"start": v(37.86, -52.9) * mm, "end": v(43.49, -52.9) * mm});
            skLineSegment(sketch, "E708", {"start": v(43.49, -52.9) * mm, "end": v(44.74, -52.07) * mm});
            skLineSegment(sketch, "E709", {"start": v(44.74, -52.07) * mm, "end": v(45.98, -51.22) * mm});
            skLineSegment(sketch, "E710", {"start": v(45.98, -51.22) * mm, "end": v(47.21, -50.35) * mm});
            skLineSegment(sketch, "E711", {"start": v(47.21, -50.35) * mm, "end": v(48.43, -49.45) * mm});
            skLineSegment(sketch, "E712", {"start": v(48.43, -49.45) * mm, "end": v(49.63, -48.52) * mm});
            skLineSegment(sketch, "E713", {"start": v(49.63, -48.52) * mm, "end": v(50.82, -47.57) * mm});
            skLineSegment(sketch, "E714", {"start": v(50.82, -47.57) * mm, "end": v(51.99, -46.58) * mm});
            skLineSegment(sketch, "E715", {"start": v(51.99, -46.58) * mm, "end": v(53.14, -45.56) * mm});
            skLineSegment(sketch, "E716", {"start": v(53.14, -45.56) * mm, "end": v(60.37, -38.21) * mm});
            skLineSegment(sketch, "E717", {"start": v(60.37, -38.21) * mm, "end": v(60.75, -37.58) * mm});
            skLineSegment(sketch, "E718", {"start": v(60.75, -37.58) * mm, "end": v(61.14, -36.92) * mm});
            skLineSegment(sketch, "E719", {"start": v(61.14, -36.92) * mm, "end": v(61.32, -36.58) * mm});
            skLineSegment(sketch, "E720", {"start": v(61.32, -36.58) * mm, "end": v(61.48, -36.24) * mm});
            skLineSegment(sketch, "E721", {"start": v(61.48, -36.24) * mm, "end": v(61.63, -35.9) * mm});
            skLineSegment(sketch, "E722", {"start": v(61.63, -35.9) * mm, "end": v(61.75, -35.55) * mm});
            skLineSegment(sketch, "E723", {"start": v(61.75, -35.55) * mm, "end": v(61.84, -35.2) * mm});
            skLineSegment(sketch, "E724", {"start": v(61.84, -35.2) * mm, "end": v(61.9, -34.84) * mm});
            skLineSegment(sketch, "E725", {"start": v(61.9, -34.84) * mm, "end": v(61.91, -34.48) * mm});
            skLineSegment(sketch, "E726", {"start": v(61.91, -34.48) * mm, "end": v(61.88, -34.13) * mm});
            skLineSegment(sketch, "E727", {"start": v(61.88, -34.13) * mm, "end": v(61.8, -33.77) * mm});
            skLineSegment(sketch, "E728", {"start": v(61.8, -33.77) * mm, "end": v(61.65, -33.41) * mm});
            skLineSegment(sketch, "E729", {"start": v(61.65, -33.41) * mm, "end": v(61.45, -33.06) * mm});
            skLineSegment(sketch, "E730", {"start": v(61.45, -33.06) * mm, "end": v(61.18, -32.7) * mm});
            skLineSegment(sketch, "E731", {"start": v(61.18, -32.7) * mm, "end": v(61.18, -21.7) * mm});
            skLineSegment(sketch, "E732", {"start": v(61.18, -21.7) * mm, "end": v(61.2, -19.95) * mm});
            skLineSegment(sketch, "E733", {"start": v(61.2, -19.95) * mm, "end": v(61.25, -18.2) * mm});
            skLineSegment(sketch, "E734", {"start": v(61.25, -18.2) * mm, "end": v(61.3, -16.44) * mm});
            skLineSegment(sketch, "E735", {"start": v(61.3, -16.44) * mm, "end": v(61.31, -14.7) * mm});
            skLineSegment(sketch, "E736", {"start": v(61.31, -14.7) * mm, "end": v(61.3, -13.83) * mm});
            skLineSegment(sketch, "E737", {"start": v(61.3, -13.83) * mm, "end": v(61.26, -12.96) * mm});
            skLineSegment(sketch, "E738", {"start": v(61.26, -12.96) * mm, "end": v(61.2, -12.1) * mm});
            skLineSegment(sketch, "E739", {"start": v(61.2, -12.1) * mm, "end": v(61.1, -11.25) * mm});
            skLineSegment(sketch, "E740", {"start": v(61.1, -11.25) * mm, "end": v(60.98, -10.4) * mm});
            skLineSegment(sketch, "E741", {"start": v(60.98, -10.4) * mm, "end": v(60.82, -9.57) * mm});
            skLineSegment(sketch, "E742", {"start": v(60.82, -9.57) * mm, "end": v(60.62, -8.74) * mm});
            skLineSegment(sketch, "E743", {"start": v(60.62, -8.74) * mm, "end": v(60.37, -7.92) * mm});
            skLineSegment(sketch, "E744", {"start": v(60.37, -7.92) * mm, "end": v(60.1, -7.47) * mm});
            skLineSegment(sketch, "E745", {"start": v(60.1, -7.47) * mm, "end": v(59.8, -7.02) * mm});
            skLineSegment(sketch, "E746", {"start": v(59.8, -7.02) * mm, "end": v(59.5, -6.58) * mm});
            skLineSegment(sketch, "E747", {"start": v(59.5, -6.58) * mm, "end": v(59.19, -6.16) * mm});
            skLineSegment(sketch, "E748", {"start": v(7.17, -3.9) * mm, "end": v(5.86, -6.03) * mm});
            skLineSegment(sketch, "E749", {"start": v(5.86, -6.03) * mm, "end": v(4.58, -8.19) * mm});
            skLineSegment(sketch, "E750", {"start": v(4.58, -8.19) * mm, "end": v(3.33, -10.36) * mm});
            skLineSegment(sketch, "E751", {"start": v(3.33, -10.36) * mm, "end": v(2.12, -12.57) * mm});
            skLineSegment(sketch, "E752", {"start": v(2.12, -12.57) * mm, "end": v(0.94, -14.8) * mm});
            skLineSegment(sketch, "E753", {"start": v(0.94, -14.8) * mm, "end": v(-0.2, -17.07) * mm});
            skLineSegment(sketch, "E754", {"start": v(-0.2, -17.07) * mm, "end": v(-1.3, -19.36) * mm});
            skLineSegment(sketch, "E755", {"start": v(-1.3, -19.36) * mm, "end": v(-2.34, -21.7) * mm});
            skLineSegment(sketch, "E756", {"start": v(-2.34, -21.7) * mm, "end": v(-3.15, -26.28) * mm});
            skLineSegment(sketch, "E757", {"start": v(-3.15, -26.28) * mm, "end": v(-3.26, -27.6) * mm});
            skLineSegment(sketch, "E758", {"start": v(-3.26, -27.6) * mm, "end": v(-3.36, -28.94) * mm});
            skLineSegment(sketch, "E759", {"start": v(-3.36, -28.94) * mm, "end": v(-3.42, -30.27) * mm});
            skLineSegment(sketch, "E760", {"start": v(-3.42, -30.27) * mm, "end": v(-3.47, -31.6) * mm});
            skLineSegment(sketch, "E761", {"start": v(-3.47, -31.6) * mm, "end": v(-3.48, -32.93) * mm});
            skLineSegment(sketch, "E762", {"start": v(-3.48, -32.93) * mm, "end": v(-3.47, -34.27) * mm});
            skLineSegment(sketch, "E763", {"start": v(-3.47, -34.27) * mm, "end": v(-3.42, -35.6) * mm});
            skLineSegment(sketch, "E764", {"start": v(-3.42, -35.6) * mm, "end": v(-3.35, -36.93) * mm});
            skLineSegment(sketch, "E765", {"start": v(-3.35, -36.93) * mm, "end": v(-3.24, -38.25) * mm});
            skLineSegment(sketch, "E766", {"start": v(-3.24, -38.25) * mm, "end": v(-3.1, -39.58) * mm});
            skLineSegment(sketch, "E767", {"start": v(-3.1, -39.58) * mm, "end": v(-2.93, -40.9) * mm});
            skLineSegment(sketch, "E768", {"start": v(-2.93, -40.9) * mm, "end": v(-2.73, -42.2) * mm});
            skLineSegment(sketch, "E769", {"start": v(-2.73, -42.2) * mm, "end": v(-2.49, -43.51) * mm});
            skLineSegment(sketch, "E770", {"start": v(-2.49, -43.51) * mm, "end": v(-2.2, -44.81) * mm});
            skLineSegment(sketch, "E771", {"start": v(-2.2, -44.81) * mm, "end": v(-1.9, -46.1) * mm});
            skLineSegment(sketch, "E772", {"start": v(-1.9, -46.1) * mm, "end": v(-1.54, -47.4) * mm});
            skLineSegment(sketch, "E773", {"start": v(-1.54, -47.4) * mm, "end": v(4.9, -55.65) * mm});
            skLineSegment(sketch, "E774", {"start": v(4.9, -55.65) * mm, "end": v(13.74, -63) * mm});
            skLineSegment(sketch, "E775", {"start": v(13.74, -63) * mm, "end": v(15.17, -64.05) * mm});
            skLineSegment(sketch, "E776", {"start": v(15.17, -64.05) * mm, "end": v(16.63, -65.06) * mm});
            skLineSegment(sketch, "E777", {"start": v(16.63, -65.06) * mm, "end": v(18.12, -66.03) * mm});
            skLineSegment(sketch, "E778", {"start": v(18.12, -66.03) * mm, "end": v(19.62, -66.95) * mm});
            skLineSegment(sketch, "E779", {"start": v(19.62, -66.95) * mm, "end": v(21.14, -67.84) * mm});
            skLineSegment(sketch, "E780", {"start": v(21.14, -67.84) * mm, "end": v(22.68, -68.7) * mm});
            skLineSegment(sketch, "E781", {"start": v(22.68, -68.7) * mm, "end": v(24.23, -69.53) * mm});
            skLineSegment(sketch, "E782", {"start": v(24.23, -69.53) * mm, "end": v(25.8, -70.34) * mm});
            skLineSegment(sketch, "E783", {"start": v(25.8, -70.34) * mm, "end": v(26.67, -70.72) * mm});
            skLineSegment(sketch, "E784", {"start": v(26.67, -70.72) * mm, "end": v(27.55, -71.05) * mm});
            skLineSegment(sketch, "E785", {"start": v(27.55, -71.05) * mm, "end": v(28.44, -71.33) * mm});
            skLineSegment(sketch, "E786", {"start": v(28.44, -71.33) * mm, "end": v(29.35, -71.57) * mm});
            skLineSegment(sketch, "E787", {"start": v(29.35, -71.57) * mm, "end": v(30.26, -71.77) * mm});
            skLineSegment(sketch, "E788", {"start": v(30.26, -71.77) * mm, "end": v(31.19, -71.93) * mm});
            skLineSegment(sketch, "E789", {"start": v(31.19, -71.93) * mm, "end": v(32.1, -72.07) * mm});
            skLineSegment(sketch, "E790", {"start": v(32.1, -72.07) * mm, "end": v(33.04, -72.17) * mm});
            skLineSegment(sketch, "E791", {"start": v(33.04, -72.17) * mm, "end": v(34.84, -72.36) * mm});
            skLineSegment(sketch, "E792", {"start": v(34.84, -72.36) * mm, "end": v(36.66, -72.53) * mm});
            skLineSegment(sketch, "E793", {"start": v(36.66, -72.53) * mm, "end": v(38.48, -72.67) * mm});
            skLineSegment(sketch, "E794", {"start": v(38.48, -72.67) * mm, "end": v(39.39, -72.72) * mm});
            skLineSegment(sketch, "E795", {"start": v(39.39, -72.72) * mm, "end": v(40.3, -72.75) * mm});
            skLineSegment(sketch, "E796", {"start": v(40.3, -72.75) * mm, "end": v(41.2, -72.77) * mm});
            skLineSegment(sketch, "E797", {"start": v(41.2, -72.77) * mm, "end": v(42.11, -72.76) * mm});
            skLineSegment(sketch, "E798", {"start": v(42.11, -72.76) * mm, "end": v(43.02, -72.73) * mm});
            skLineSegment(sketch, "E799", {"start": v(43.02, -72.73) * mm, "end": v(43.92, -72.68) * mm});
            skLineSegment(sketch, "E800", {"start": v(43.92, -72.68) * mm, "end": v(44.82, -72.6) * mm});
            skLineSegment(sketch, "E801", {"start": v(44.82, -72.6) * mm, "end": v(45.72, -72.5) * mm});
            skLineSegment(sketch, "E802", {"start": v(45.72, -72.5) * mm, "end": v(46.62, -72.35) * mm});
            skLineSegment(sketch, "E803", {"start": v(46.62, -72.35) * mm, "end": v(47.5, -72.17) * mm});
            skLineSegment(sketch, "E804", {"start": v(47.5, -72.17) * mm, "end": v(53.94, -68.5) * mm});
            skLineSegment(sketch, "E805", {"start": v(53.94, -68.5) * mm, "end": v(69.22, -57.49) * mm});
            skLineSegment(sketch, "E806", {"start": v(69.22, -57.49) * mm, "end": v(69.5, -57.16) * mm});
            skLineSegment(sketch, "E807", {"start": v(69.5, -57.16) * mm, "end": v(69.76, -56.8) * mm});
            skLineSegment(sketch, "E808", {"start": v(69.76, -56.8) * mm, "end": v(70.01, -56.45) * mm});
            skLineSegment(sketch, "E809", {"start": v(70.01, -56.45) * mm, "end": v(70.25, -56.08) * mm});
            skLineSegment(sketch, "E810", {"start": v(70.25, -56.08) * mm, "end": v(70.69, -55.31) * mm});
            skLineSegment(sketch, "E811", {"start": v(70.69, -55.31) * mm, "end": v(71.09, -54.5) * mm});
            skLineSegment(sketch, "E812", {"start": v(71.09, -54.5) * mm, "end": v(71.46, -53.67) * mm});
            skLineSegment(sketch, "E813", {"start": v(71.46, -53.67) * mm, "end": v(71.8, -52.82) * mm});
            skLineSegment(sketch, "E814", {"start": v(71.8, -52.82) * mm, "end": v(72.12, -51.94) * mm});
            skLineSegment(sketch, "E815", {"start": v(72.12, -51.94) * mm, "end": v(72.43, -51.06) * mm});
            skLineSegment(sketch, "E816", {"start": v(72.43, -51.06) * mm, "end": v(74.85, -34.54) * mm});
            skLineSegment(sketch, "E817", {"start": v(74.85, -34.54) * mm, "end": v(74.92, -33.28) * mm});
            skLineSegment(sketch, "E818", {"start": v(74.92, -33.28) * mm, "end": v(74.98, -32.02) * mm});
            skLineSegment(sketch, "E819", {"start": v(74.98, -32.02) * mm, "end": v(75.02, -30.76) * mm});
            skLineSegment(sketch, "E820", {"start": v(75.02, -30.76) * mm, "end": v(75.04, -29.5) * mm});
            skLineSegment(sketch, "E821", {"start": v(75.04, -29.5) * mm, "end": v(75.05, -26.98) * mm});
            skLineSegment(sketch, "E822", {"start": v(75.05, -26.98) * mm, "end": v(75.02, -24.45) * mm});
            skLineSegment(sketch, "E823", {"start": v(75.02, -24.45) * mm, "end": v(74.91, -19.4) * mm});
            skLineSegment(sketch, "E824", {"start": v(74.91, -19.4) * mm, "end": v(74.86, -16.87) * mm});
            skLineSegment(sketch, "E825", {"start": v(74.86, -16.87) * mm, "end": v(74.85, -14.35) * mm});
            skLineSegment(sketch, "E826", {"start": v(74.85, -14.35) * mm, "end": v(74.52, -14) * mm});
            skLineSegment(sketch, "E827", {"start": v(74.52, -14) * mm, "end": v(74.34, -13.85) * mm});
            skLineSegment(sketch, "E828", {"start": v(74.34, -13.85) * mm, "end": v(74.16, -13.7) * mm});
            skLineSegment(sketch, "E829", {"start": v(74.16, -13.7) * mm, "end": v(73.96, -13.6) * mm});
            skLineSegment(sketch, "E830", {"start": v(73.96, -13.6) * mm, "end": v(73.74, -13.5) * mm});
            skLineSegment(sketch, "E831", {"start": v(73.74, -13.5) * mm, "end": v(73.5, -13.45) * mm});
            skLineSegment(sketch, "E832", {"start": v(73.5, -13.45) * mm, "end": v(73.24, -13.43) * mm});
            skLineSegment(sketch, "E833", {"start": v(73.24, -13.43) * mm, "end": v(71.63, -15.27) * mm});
            skLineSegment(sketch, "E834", {"start": v(71.63, -15.27) * mm, "end": v(71.48, -15.45) * mm});
            skLineSegment(sketch, "E835", {"start": v(71.48, -15.45) * mm, "end": v(71.34, -15.65) * mm});
            skLineSegment(sketch, "E836", {"start": v(71.34, -15.65) * mm, "end": v(71.09, -16.06) * mm});
            skLineSegment(sketch, "E837", {"start": v(71.09, -16.06) * mm, "end": v(70.87, -16.5) * mm});
            skLineSegment(sketch, "E838", {"start": v(70.87, -16.5) * mm, "end": v(70.69, -16.98) * mm});
            skLineSegment(sketch, "E839", {"start": v(70.69, -16.98) * mm, "end": v(70.35, -17.95) * mm});
            skLineSegment(sketch, "E840", {"start": v(70.35, -17.95) * mm, "end": v(70.02, -18.94) * mm});
            skLineSegment(sketch, "E841", {"start": v(70.02, -18.94) * mm, "end": v(69.32, -21.5) * mm});
            skLineSegment(sketch, "E842", {"start": v(69.32, -21.5) * mm, "end": v(68.6, -24.06) * mm});
            skLineSegment(sketch, "E843", {"start": v(68.6, -24.06) * mm, "end": v(67.85, -26.6) * mm});
            skLineSegment(sketch, "E844", {"start": v(67.85, -26.6) * mm, "end": v(67.07, -29.14) * mm});
            skLineSegment(sketch, "E845", {"start": v(67.07, -29.14) * mm, "end": v(66.26, -31.66) * mm});
            skLineSegment(sketch, "E846", {"start": v(66.26, -31.66) * mm, "end": v(65.41, -34.17) * mm});
            skLineSegment(sketch, "E847", {"start": v(65.41, -34.17) * mm, "end": v(64.52, -36.66) * mm});
            skLineSegment(sketch, "E848", {"start": v(64.52, -36.66) * mm, "end": v(63.59, -39.13) * mm});
            skLineSegment(sketch, "E849", {"start": v(63.59, -39.13) * mm, "end": v(62.87, -40.35) * mm});
            skLineSegment(sketch, "E850", {"start": v(62.87, -40.35) * mm, "end": v(62.13, -41.55) * mm});
            skLineSegment(sketch, "E851", {"start": v(62.13, -41.55) * mm, "end": v(61.36, -42.73) * mm});
            skLineSegment(sketch, "E852", {"start": v(61.36, -42.73) * mm, "end": v(60.58, -43.9) * mm});
            skLineSegment(sketch, "E853", {"start": v(60.58, -43.9) * mm, "end": v(59.77, -45.03) * mm});
            skLineSegment(sketch, "E854", {"start": v(59.77, -45.03) * mm, "end": v(58.93, -46.15) * mm});
            skLineSegment(sketch, "E855", {"start": v(58.93, -46.15) * mm, "end": v(58.06, -47.25) * mm});
            skLineSegment(sketch, "E856", {"start": v(58.06, -47.25) * mm, "end": v(57.16, -48.31) * mm});
            skLineSegment(sketch, "E857", {"start": v(57.16, -48.31) * mm, "end": v(46.7, -55.65) * mm});
            skLineSegment(sketch, "E858", {"start": v(46.7, -55.65) * mm, "end": v(42.68, -57.49) * mm});
            skLineSegment(sketch, "E859", {"start": v(42.68, -57.49) * mm, "end": v(42.34, -57.55) * mm});
            skLineSegment(sketch, "E860", {"start": v(42.34, -57.55) * mm, "end": v(41.99, -57.6) * mm});
            skLineSegment(sketch, "E861", {"start": v(41.99, -57.6) * mm, "end": v(41.29, -57.65) * mm});
            skLineSegment(sketch, "E862", {"start": v(41.29, -57.65) * mm, "end": v(40.59, -57.65) * mm});
            skLineSegment(sketch, "E863", {"start": v(40.59, -57.65) * mm, "end": v(39.88, -57.63) * mm});
            skLineSegment(sketch, "E864", {"start": v(39.88, -57.63) * mm, "end": v(38.47, -57.54) * mm});
            skLineSegment(sketch, "E865", {"start": v(38.47, -57.54) * mm, "end": v(37.76, -57.5) * mm});
            skLineSegment(sketch, "E866", {"start": v(37.76, -57.5) * mm, "end": v(37.06, -57.49) * mm});
            skLineSegment(sketch, "E867", {"start": v(37.06, -57.49) * mm, "end": v(18.56, -40.97) * mm});
            skLineSegment(sketch, "E868", {"start": v(18.56, -40.97) * mm, "end": v(13.74, -39.13) * mm});
            skLineSegment(sketch, "E869", {"start": v(13.74, -39.13) * mm, "end": v(13.36, -38.92) * mm});
            skLineSegment(sketch, "E870", {"start": v(13.36, -38.92) * mm, "end": v(13, -38.67) * mm});
            skLineSegment(sketch, "E871", {"start": v(13, -38.67) * mm, "end": v(12.66, -38.38) * mm});
            skLineSegment(sketch, "E872", {"start": v(12.66, -38.38) * mm, "end": v(12.35, -38.05) * mm});
            skLineSegment(sketch, "E873", {"start": v(12.35, -38.05) * mm, "end": v(12.06, -37.69) * mm});
            skLineSegment(sketch, "E874", {"start": v(12.06, -37.69) * mm, "end": v(11.8, -37.28) * mm});
            skLineSegment(sketch, "E875", {"start": v(11.8, -37.28) * mm, "end": v(11.55, -36.85) * mm});
            skLineSegment(sketch, "E876", {"start": v(11.55, -36.85) * mm, "end": v(11.33, -36.38) * mm});
            skLineSegment(sketch, "E877", {"start": v(11.33, -36.38) * mm, "end": v(10, -8.36) * mm});
            skLineSegment(sketch, "E878", {"start": v(37.04, -19.96) * mm, "end": v(37.02, -20.39) * mm});
            skLineSegment(sketch, "E879", {"start": v(37.02, -20.39) * mm, "end": v(37.02, -20.83) * mm});
            skLineSegment(sketch, "E880", {"start": v(37.02, -20.83) * mm, "end": v(37.05, -21.72) * mm});
            skLineSegment(sketch, "E881", {"start": v(37.05, -21.72) * mm, "end": v(37.13, -22.64) * mm});
            skLineSegment(sketch, "E882", {"start": v(37.13, -22.64) * mm, "end": v(37.24, -23.57) * mm});
            skLineSegment(sketch, "E883", {"start": v(37.24, -23.57) * mm, "end": v(37.38, -24.5) * mm});
            skLineSegment(sketch, "E884", {"start": v(37.38, -24.5) * mm, "end": v(37.54, -25.42) * mm});
            skLineSegment(sketch, "E885", {"start": v(37.54, -25.42) * mm, "end": v(37.86, -27.2) * mm});
            skLineSegment(sketch, "E886", {"start": v(37.86, -27.2) * mm, "end": v(38.38, -27.8) * mm});
            skLineSegment(sketch, "E887", {"start": v(38.38, -27.8) * mm, "end": v(38.92, -28.38) * mm});
            skLineSegment(sketch, "E888", {"start": v(38.92, -28.38) * mm, "end": v(39.47, -28.95) * mm});
            skLineSegment(sketch, "E889", {"start": v(39.47, -28.95) * mm, "end": v(40.04, -29.48) * mm});
            skLineSegment(sketch, "E890", {"start": v(40.04, -29.48) * mm, "end": v(40.34, -29.73) * mm});
            skLineSegment(sketch, "E891", {"start": v(40.34, -29.73) * mm, "end": v(40.65, -29.96) * mm});
            skLineSegment(sketch, "E892", {"start": v(40.65, -29.96) * mm, "end": v(40.96, -30.17) * mm});
            skLineSegment(sketch, "E893", {"start": v(40.96, -30.17) * mm, "end": v(41.28, -30.36) * mm});
            skLineSegment(sketch, "E894", {"start": v(41.28, -30.36) * mm, "end": v(41.62, -30.52) * mm});
            skLineSegment(sketch, "E895", {"start": v(41.62, -30.52) * mm, "end": v(41.96, -30.67) * mm});
            skLineSegment(sketch, "E896", {"start": v(41.96, -30.67) * mm, "end": v(42.32, -30.78) * mm});
            skLineSegment(sketch, "E897", {"start": v(42.32, -30.78) * mm, "end": v(42.68, -30.87) * mm});
            skLineSegment(sketch, "E898", {"start": v(42.68, -30.87) * mm, "end": v(46.7, -30.87) * mm});
            skLineSegment(sketch, "E899", {"start": v(46.7, -30.87) * mm, "end": v(48.31, -28.12) * mm});
            skLineSegment(sketch, "E900", {"start": v(48.31, -28.12) * mm, "end": v(48.34, -26.74) * mm});
            skLineSegment(sketch, "E901", {"start": v(48.34, -26.74) * mm, "end": v(48.4, -25.35) * mm});
            skLineSegment(sketch, "E902", {"start": v(48.4, -25.35) * mm, "end": v(48.53, -22.59) * mm});
            skLineSegment(sketch, "E903", {"start": v(48.53, -22.59) * mm, "end": v(48.57, -21.2) * mm});
            skLineSegment(sketch, "E904", {"start": v(48.57, -21.2) * mm, "end": v(48.57, -20.52) * mm});
            skLineSegment(sketch, "E905", {"start": v(48.57, -20.52) * mm, "end": v(48.56, -19.83) * mm});
            skLineSegment(sketch, "E906", {"start": v(48.56, -19.83) * mm, "end": v(48.53, -19.15) * mm});
            skLineSegment(sketch, "E907", {"start": v(48.53, -19.15) * mm, "end": v(48.48, -18.46) * mm});
            skLineSegment(sketch, "E908", {"start": v(48.48, -18.46) * mm, "end": v(48.4, -17.78) * mm});
            skLineSegment(sketch, "E909", {"start": v(48.4, -17.78) * mm, "end": v(48.31, -17.1) * mm});
            skLineSegment(sketch, "E910", {"start": v(48.31, -17.1) * mm, "end": v(48.14, -16.5) * mm});
            skLineSegment(sketch, "E911", {"start": v(-16.01, -27.2) * mm, "end": v(-17.33, -27.22) * mm});
            skLineSegment(sketch, "E912", {"start": v(-17.33, -27.22) * mm, "end": v(-18.65, -27.3) * mm});
            skLineSegment(sketch, "E913", {"start": v(-18.65, -27.3) * mm, "end": v(-19.96, -27.43) * mm});
            skLineSegment(sketch, "E914", {"start": v(-19.96, -27.43) * mm, "end": v(-20.62, -27.52) * mm});
            skLineSegment(sketch, "E915", {"start": v(-20.62, -27.52) * mm, "end": v(-21.27, -27.63) * mm});
            skLineSegment(sketch, "E916", {"start": v(-21.27, -27.63) * mm, "end": v(-21.92, -27.74) * mm});
            skLineSegment(sketch, "E917", {"start": v(-21.92, -27.74) * mm, "end": v(-22.58, -27.88) * mm});
            skLineSegment(sketch, "E918", {"start": v(-22.58, -27.88) * mm, "end": v(-23.23, -28.03) * mm});
            skLineSegment(sketch, "E919", {"start": v(-23.23, -28.03) * mm, "end": v(-23.88, -28.2) * mm});
            skLineSegment(sketch, "E920", {"start": v(-23.88, -28.2) * mm, "end": v(-24.52, -28.38) * mm});
            skLineSegment(sketch, "E921", {"start": v(-24.52, -28.38) * mm, "end": v(-25.17, -28.58) * mm});
            skLineSegment(sketch, "E922", {"start": v(-25.17, -28.58) * mm, "end": v(-25.82, -28.8) * mm});
            skLineSegment(sketch, "E923", {"start": v(-25.82, -28.8) * mm, "end": v(-26.46, -29.03) * mm});
            skLineSegment(sketch, "E924", {"start": v(-26.46, -29.03) * mm, "end": v(-28.07, -30.87) * mm});
            skLineSegment(sketch, "E925", {"start": v(-28.07, -30.87) * mm, "end": v(-28.05, -31.17) * mm});
            skLineSegment(sketch, "E926", {"start": v(-28.05, -31.17) * mm, "end": v(-28, -31.46) * mm});
            skLineSegment(sketch, "E927", {"start": v(-28, -31.46) * mm, "end": v(-27.9, -31.73) * mm});
            skLineSegment(sketch, "E928", {"start": v(-27.9, -31.73) * mm, "end": v(-27.76, -31.99) * mm});
            skLineSegment(sketch, "E929", {"start": v(-27.76, -31.99) * mm, "end": v(-27.6, -32.24) * mm});
            skLineSegment(sketch, "E930", {"start": v(-27.6, -32.24) * mm, "end": v(-27.42, -32.48) * mm});
            skLineSegment(sketch, "E931", {"start": v(-27.42, -32.48) * mm, "end": v(-27.2, -32.7) * mm});
            skLineSegment(sketch, "E932", {"start": v(-27.2, -32.7) * mm, "end": v(-26.98, -32.93) * mm});
            skLineSegment(sketch, "E933", {"start": v(-26.98, -32.93) * mm, "end": v(-26.48, -33.35) * mm});
            skLineSegment(sketch, "E934", {"start": v(-26.48, -33.35) * mm, "end": v(-25.94, -33.76) * mm});
            skLineSegment(sketch, "E935", {"start": v(-25.94, -33.76) * mm, "end": v(-25.39, -34.15) * mm});
            skLineSegment(sketch, "E936", {"start": v(-25.39, -34.15) * mm, "end": v(-24.86, -34.54) * mm});
            skLineSegment(sketch, "E937", {"start": v(-24.86, -34.54) * mm, "end": v(-21.64, -38.21) * mm});
            skLineSegment(sketch, "E938", {"start": v(-21.64, -38.21) * mm, "end": v(-21.15, -38.8) * mm});
            skLineSegment(sketch, "E939", {"start": v(-21.15, -38.8) * mm, "end": v(-20.7, -39.44) * mm});
            skLineSegment(sketch, "E940", {"start": v(-20.7, -39.44) * mm, "end": v(-20.28, -40.1) * mm});
            skLineSegment(sketch, "E941", {"start": v(-20.28, -40.1) * mm, "end": v(-19.9, -40.77) * mm});
            skLineSegment(sketch, "E942", {"start": v(-19.9, -40.77) * mm, "end": v(-19.54, -41.48) * mm});
            skLineSegment(sketch, "E943", {"start": v(-19.54, -41.48) * mm, "end": v(-19.2, -42.2) * mm});
            skLineSegment(sketch, "E944", {"start": v(-19.2, -42.2) * mm, "end": v(-18.9, -42.95) * mm});
            skLineSegment(sketch, "E945", {"start": v(-18.9, -42.95) * mm, "end": v(-18.62, -43.72) * mm});
            skLineSegment(sketch, "E946", {"start": v(-18.62, -43.72) * mm, "end": v(-18.35, -44.5) * mm});
            skLineSegment(sketch, "E947", {"start": v(-18.35, -44.5) * mm, "end": v(-18.1, -45.28) * mm});
            skLineSegment(sketch, "E948", {"start": v(-18.1, -45.28) * mm, "end": v(-17.64, -46.9) * mm});
            skLineSegment(sketch, "E949", {"start": v(-17.64, -46.9) * mm, "end": v(-17.22, -48.52) * mm});
            skLineSegment(sketch, "E950", {"start": v(-17.22, -48.52) * mm, "end": v(-16.82, -50.15) * mm});
            skLineSegment(sketch, "E951", {"start": v(-16.82, -50.15) * mm, "end": v(-15.2, -65.75) * mm});
            skLineSegment(sketch, "E952", {"start": v(-15.2, -65.75) * mm, "end": v(-12, -74.01) * mm});
            skLineSegment(sketch, "E953", {"start": v(-12, -74.01) * mm, "end": v(-11.3, -74.75) * mm});
            skLineSegment(sketch, "E954", {"start": v(-11.3, -74.75) * mm, "end": v(-10.57, -75.45) * mm});
            skLineSegment(sketch, "E955", {"start": v(-10.57, -75.45) * mm, "end": v(-9.81, -76.1) * mm});
            skLineSegment(sketch, "E956", {"start": v(-9.81, -76.1) * mm, "end": v(-9.02, -76.7) * mm});
            skLineSegment(sketch, "E957", {"start": v(-9.02, -76.7) * mm, "end": v(-8.19, -77.25) * mm});
            skLineSegment(sketch, "E958", {"start": v(-8.19, -77.25) * mm, "end": v(-7.34, -77.75) * mm});
            skLineSegment(sketch, "E959", {"start": v(-7.34, -77.75) * mm, "end": v(-6.46, -78.2) * mm});
            skLineSegment(sketch, "E960", {"start": v(-6.46, -78.2) * mm, "end": v(-5.56, -78.6) * mm});
            skLineSegment(sketch, "E961", {"start": v(-5.56, -78.6) * mm, "end": v(-3.05, -79.17) * mm});
            skLineSegment(sketch, "E962", {"start": v(-3.05, -79.17) * mm, "end": v(-0.54, -79.77) * mm});
            skLineSegment(sketch, "E963", {"start": v(-0.54, -79.77) * mm, "end": v(0.71, -80.1) * mm});
            skLineSegment(sketch, "E964", {"start": v(0.71, -80.1) * mm, "end": v(1.96, -80.44) * mm});
            skLineSegment(sketch, "E965", {"start": v(1.96, -80.44) * mm, "end": v(3.2, -80.8) * mm});
            skLineSegment(sketch, "E966", {"start": v(3.2, -80.8) * mm, "end": v(4.43, -81.2) * mm});
            skLineSegment(sketch, "E967", {"start": v(4.43, -81.2) * mm, "end": v(5.65, -81.63) * mm});
            skLineSegment(sketch, "E968", {"start": v(5.65, -81.63) * mm, "end": v(6.86, -82.1) * mm});
            skLineSegment(sketch, "E969", {"start": v(6.86, -82.1) * mm, "end": v(8.05, -82.6) * mm});
            skLineSegment(sketch, "E970", {"start": v(8.05, -82.6) * mm, "end": v(9.23, -83.16) * mm});
            skLineSegment(sketch, "E971", {"start": v(9.23, -83.16) * mm, "end": v(10.39, -83.77) * mm});
            skLineSegment(sketch, "E972", {"start": v(10.39, -83.77) * mm, "end": v(10.96, -84.1) * mm});
            skLineSegment(sketch, "E973", {"start": v(10.96, -84.1) * mm, "end": v(11.53, -84.43) * mm});
            skLineSegment(sketch, "E974", {"start": v(11.53, -84.43) * mm, "end": v(12.09, -84.78) * mm});
            skLineSegment(sketch, "E975", {"start": v(12.09, -84.78) * mm, "end": v(12.64, -85.15) * mm});
            skLineSegment(sketch, "E976", {"start": v(12.64, -85.15) * mm, "end": v(13.2, -85.54) * mm});
            skLineSegment(sketch, "E977", {"start": v(13.2, -85.54) * mm, "end": v(13.74, -85.94) * mm});
            skLineSegment(sketch, "E978", {"start": v(13.74, -85.94) * mm, "end": v(20.17, -89.61) * mm});
            skLineSegment(sketch, "E979", {"start": v(20.17, -89.61) * mm, "end": v(21.18, -89.64) * mm});
            skLineSegment(sketch, "E980", {"start": v(21.18, -89.64) * mm, "end": v(22.19, -89.7) * mm});
            skLineSegment(sketch, "E981", {"start": v(22.19, -89.7) * mm, "end": v(24.2, -89.82) * mm});
            skLineSegment(sketch, "E982", {"start": v(24.2, -89.82) * mm, "end": v(25.21, -89.85) * mm});
            skLineSegment(sketch, "E983", {"start": v(25.21, -89.85) * mm, "end": v(26.22, -89.84) * mm});
            skLineSegment(sketch, "E984", {"start": v(26.22, -89.84) * mm, "end": v(26.72, -89.82) * mm});
            skLineSegment(sketch, "E985", {"start": v(26.72, -89.82) * mm, "end": v(27.22, -89.77) * mm});
            skLineSegment(sketch, "E986", {"start": v(27.22, -89.77) * mm, "end": v(27.72, -89.7) * mm});
            skLineSegment(sketch, "E987", {"start": v(27.72, -89.7) * mm, "end": v(28.21, -89.61) * mm});
            skLineSegment(sketch, "E988", {"start": v(28.21, -89.61) * mm, "end": v(28.8, -89.46) * mm});
            skLineSegment(sketch, "E989", {"start": v(28.8, -89.46) * mm, "end": v(29.38, -89.26) * mm});
            skLineSegment(sketch, "E990", {"start": v(29.38, -89.26) * mm, "end": v(29.95, -89) * mm});
            skLineSegment(sketch, "E991", {"start": v(29.95, -89) * mm, "end": v(30.5, -88.71) * mm});
            skLineSegment(sketch, "E992", {"start": v(30.5, -88.71) * mm, "end": v(31.02, -88.38) * mm});
            skLineSegment(sketch, "E993", {"start": v(31.02, -88.38) * mm, "end": v(31.54, -88) * mm});
            skLineSegment(sketch, "E994", {"start": v(31.54, -88) * mm, "end": v(32.05, -87.6) * mm});
            skLineSegment(sketch, "E995", {"start": v(32.05, -87.6) * mm, "end": v(32.55, -87.17) * mm});
            skLineSegment(sketch, "E996", {"start": v(32.55, -87.17) * mm, "end": v(33.03, -86.71) * mm});
            skLineSegment(sketch, "E997", {"start": v(33.03, -86.71) * mm, "end": v(33.51, -86.24) * mm});
            skLineSegment(sketch, "E998", {"start": v(33.51, -86.24) * mm, "end": v(34.44, -85.25) * mm});
            skLineSegment(sketch, "E999", {"start": v(34.44, -85.25) * mm, "end": v(35.36, -84.22) * mm});
            skLineSegment(sketch, "E1000", {"start": v(35.36, -84.22) * mm, "end": v(36.25, -83.19) * mm});
            skLineSegment(sketch, "E1001", {"start": v(36.25, -83.19) * mm, "end": v(37.03, -82.48) * mm});
            skLineSegment(sketch, "E1002", {"start": v(37.03, -82.48) * mm, "end": v(37.8, -81.75) * mm});
            skLineSegment(sketch, "E1003", {"start": v(37.8, -81.75) * mm, "end": v(38.54, -81.01) * mm});
            skLineSegment(sketch, "E1004", {"start": v(38.54, -81.01) * mm, "end": v(39.27, -80.24) * mm});
            skLineSegment(sketch, "E1005", {"start": v(39.27, -80.24) * mm, "end": v(39.98, -79.44) * mm});
            skLineSegment(sketch, "E1006", {"start": v(39.98, -79.44) * mm, "end": v(40.65, -78.6) * mm});
            skLineSegment(sketch, "E1007", {"start": v(40.65, -78.6) * mm, "end": v(40.97, -78.16) * mm});
            skLineSegment(sketch, "E1008", {"start": v(40.97, -78.16) * mm, "end": v(41.29, -77.7) * mm});
            skLineSegment(sketch, "E1009", {"start": v(41.29, -77.7) * mm, "end": v(41.59, -77.24) * mm});
            skLineSegment(sketch, "E1010", {"start": v(41.59, -77.24) * mm, "end": v(41.88, -76.76) * mm});
            skLineSegment(sketch, "E1011", {"start": v(41.88, -76.76) * mm, "end": v(41.88, -75.85) * mm});
            skLineSegment(sketch, "E1012", {"start": v(41.88, -75.85) * mm, "end": v(39.66, -75.48) * mm});
            skLineSegment(sketch, "E1013", {"start": v(39.66, -75.48) * mm, "end": v(37.43, -75.1) * mm});
            skLineSegment(sketch, "E1014", {"start": v(37.43, -75.1) * mm, "end": v(35.21, -74.7) * mm});
            skLineSegment(sketch, "E1015", {"start": v(35.21, -74.7) * mm, "end": v(33, -74.27) * mm});
            skLineSegment(sketch, "E1016", {"start": v(33, -74.27) * mm, "end": v(30.79, -73.81) * mm});
            skLineSegment(sketch, "E1017", {"start": v(30.79, -73.81) * mm, "end": v(28.58, -73.31) * mm});
            skLineSegment(sketch, "E1018", {"start": v(28.58, -73.31) * mm, "end": v(26.38, -72.77) * mm});
            skLineSegment(sketch, "E1019", {"start": v(26.38, -72.77) * mm, "end": v(24.2, -72.17) * mm});
            skLineSegment(sketch, "E1020", {"start": v(24.2, -72.17) * mm, "end": v(22.63, -71.37) * mm});
            skLineSegment(sketch, "E1021", {"start": v(22.63, -71.37) * mm, "end": v(21.09, -70.55) * mm});
            skLineSegment(sketch, "E1022", {"start": v(21.09, -70.55) * mm, "end": v(19.55, -69.7) * mm});
            skLineSegment(sketch, "E1023", {"start": v(19.55, -69.7) * mm, "end": v(18.03, -68.8) * mm});
            skLineSegment(sketch, "E1024", {"start": v(18.03, -68.8) * mm, "end": v(16.53, -67.88) * mm});
            skLineSegment(sketch, "E1025", {"start": v(16.53, -67.88) * mm, "end": v(15.04, -66.9) * mm});
            skLineSegment(sketch, "E1026", {"start": v(15.04, -66.9) * mm, "end": v(13.58, -65.9) * mm});
            skLineSegment(sketch, "E1027", {"start": v(13.58, -65.9) * mm, "end": v(12.13, -64.83) * mm});
            skLineSegment(sketch, "E1028", {"start": v(12.13, -64.83) * mm, "end": v(3.29, -57.49) * mm});
            skLineSegment(sketch, "E1029", {"start": v(3.29, -57.49) * mm, "end": v(-3.15, -49.23) * mm});
            skLineSegment(sketch, "E1030", {"start": v(-3.15, -49.23) * mm, "end": v(-3.68, -48.28) * mm});
            skLineSegment(sketch, "E1031", {"start": v(-3.68, -48.28) * mm, "end": v(-4.18, -47.31) * mm});
            skLineSegment(sketch, "E1032", {"start": v(-4.18, -47.31) * mm, "end": v(-4.65, -46.33) * mm});
            skLineSegment(sketch, "E1033", {"start": v(-4.65, -46.33) * mm, "end": v(-5.1, -45.33) * mm});
            skLineSegment(sketch, "E1034", {"start": v(-5.1, -45.33) * mm, "end": v(-5.53, -44.32) * mm});
            skLineSegment(sketch, "E1035", {"start": v(-5.53, -44.32) * mm, "end": v(-5.94, -43.29) * mm});
            skLineSegment(sketch, "E1036", {"start": v(-5.94, -43.29) * mm, "end": v(-6.34, -42.25) * mm});
            skLineSegment(sketch, "E1037", {"start": v(-6.34, -42.25) * mm, "end": v(-6.72, -41.2) * mm});
            skLineSegment(sketch, "E1038", {"start": v(-6.72, -41.2) * mm, "end": v(-7.45, -39.09) * mm});
            skLineSegment(sketch, "E1039", {"start": v(-7.45, -39.09) * mm, "end": v(-8.15, -36.96) * mm});
            skLineSegment(sketch, "E1040", {"start": v(-8.15, -36.96) * mm, "end": v(-8.86, -34.83) * mm});
            skLineSegment(sketch, "E1041", {"start": v(-8.86, -34.83) * mm, "end": v(-9.58, -32.7) * mm});
            skLineSegment(sketch, "E1042", {"start": v(-9.58, -32.7) * mm, "end": v(-10.3, -31.9) * mm});
            skLineSegment(sketch, "E1043", {"start": v(-10.3, -31.9) * mm, "end": v(-11.04, -31.13) * mm});
            skLineSegment(sketch, "E1044", {"start": v(-11.04, -31.13) * mm, "end": v(-11.8, -30.38) * mm});
            skLineSegment(sketch, "E1045", {"start": v(-11.8, -30.38) * mm, "end": v(-12.58, -29.67) * mm});
            skLineSegment(sketch, "E1046", {"start": v(-12.58, -29.67) * mm, "end": v(-13.4, -29) * mm});
            skLineSegment(sketch, "E1047", {"start": v(-13.4, -29) * mm, "end": v(-14.23, -28.35) * mm});
            skLineSegment(sketch, "E1048", {"start": v(-14.23, -28.35) * mm, "end": v(-15.1, -27.75) * mm});
            skLineSegment(sketch, "E1049", {"start": v(-15.1, -27.75) * mm, "end": v(-15.55, -27.47) * mm});
            skLineSegment(sketch, "E1050", {"start": v(-15.55, -27.47) * mm, "end": v(-16.01, -27.2) * mm});
            skLineSegment(sketch, "E1051", {"start": v(92.53, -32.7) * mm, "end": v(92.36, -32.72) * mm});
            skLineSegment(sketch, "E1052", {"start": v(92.36, -32.72) * mm, "end": v(92.19, -32.75) * mm});
            skLineSegment(sketch, "E1053", {"start": v(92.19, -32.75) * mm, "end": v(92.03, -32.8) * mm});
            skLineSegment(sketch, "E1054", {"start": v(92.03, -32.8) * mm, "end": v(91.88, -32.88) * mm});
            skLineSegment(sketch, "E1055", {"start": v(91.88, -32.88) * mm, "end": v(91.73, -32.97) * mm});
            skLineSegment(sketch, "E1056", {"start": v(91.73, -32.97) * mm, "end": v(91.6, -33.08) * mm});
            skLineSegment(sketch, "E1057", {"start": v(91.6, -33.08) * mm, "end": v(91.46, -33.21) * mm});
            skLineSegment(sketch, "E1058", {"start": v(91.46, -33.21) * mm, "end": v(91.34, -33.36) * mm});
            skLineSegment(sketch, "E1059", {"start": v(91.34, -33.36) * mm, "end": v(91.1, -33.7) * mm});
            skLineSegment(sketch, "E1060", {"start": v(91.1, -33.7) * mm, "end": v(90.9, -34.08) * mm});
            skLineSegment(sketch, "E1061", {"start": v(90.9, -34.08) * mm, "end": v(90.7, -34.5) * mm});
            skLineSegment(sketch, "E1062", {"start": v(90.7, -34.5) * mm, "end": v(90.53, -34.98) * mm});
            skLineSegment(sketch, "E1063", {"start": v(90.53, -34.98) * mm, "end": v(90.37, -35.47) * mm});
            skLineSegment(sketch, "E1064", {"start": v(90.37, -35.47) * mm, "end": v(90.21, -36) * mm});
            skLineSegment(sketch, "E1065", {"start": v(90.21, -36) * mm, "end": v(89.92, -37.07) * mm});
            skLineSegment(sketch, "E1066", {"start": v(89.92, -37.07) * mm, "end": v(89.63, -38.13) * mm});
            skLineSegment(sketch, "E1067", {"start": v(89.63, -38.13) * mm, "end": v(89.48, -38.65) * mm});
            skLineSegment(sketch, "E1068", {"start": v(89.48, -38.65) * mm, "end": v(89.32, -39.13) * mm});
            skLineSegment(sketch, "E1069", {"start": v(89.32, -39.13) * mm, "end": v(82.89, -51.98) * mm});
            skLineSegment(sketch, "E1070", {"start": v(82.89, -51.98) * mm, "end": v(81.53, -52.99) * mm});
            skLineSegment(sketch, "E1071", {"start": v(81.53, -52.99) * mm, "end": v(80.17, -53.96) * mm});
            skLineSegment(sketch, "E1072", {"start": v(80.17, -53.96) * mm, "end": v(78.79, -54.91) * mm});
            skLineSegment(sketch, "E1073", {"start": v(78.79, -54.91) * mm, "end": v(77.4, -55.84) * mm});
            skLineSegment(sketch, "E1074", {"start": v(77.4, -55.84) * mm, "end": v(75.98, -56.75) * mm});
            skLineSegment(sketch, "E1075", {"start": v(75.98, -56.75) * mm, "end": v(74.57, -57.65) * mm});
            skLineSegment(sketch, "E1076", {"start": v(74.57, -57.65) * mm, "end": v(71.72, -59.42) * mm});
            skLineSegment(sketch, "E1077", {"start": v(71.72, -59.42) * mm, "end": v(68.86, -61.17) * mm});
            skLineSegment(sketch, "E1078", {"start": v(68.86, -61.17) * mm, "end": v(66, -62.94) * mm});
            skLineSegment(sketch, "E1079", {"start": v(66, -62.94) * mm, "end": v(64.59, -63.85) * mm});
            skLineSegment(sketch, "E1080", {"start": v(64.59, -63.85) * mm, "end": v(63.17, -64.77) * mm});
            skLineSegment(sketch, "E1081", {"start": v(63.17, -64.77) * mm, "end": v(61.77, -65.7) * mm});
            skLineSegment(sketch, "E1082", {"start": v(61.77, -65.7) * mm, "end": v(60.37, -66.67) * mm});
            skLineSegment(sketch, "E1083", {"start": v(60.37, -66.67) * mm, "end": v(51.53, -74.01) * mm});
            skLineSegment(sketch, "E1084", {"start": v(51.53, -74.01) * mm, "end": v(44.3, -77.68) * mm});
            skLineSegment(sketch, "E1085", {"start": v(44.3, -77.68) * mm, "end": v(41.08, -84.1) * mm});
            skLineSegment(sketch, "E1086", {"start": v(41.08, -84.1) * mm, "end": v(41.08, -89.61) * mm});
            skLineSegment(sketch, "E1087", {"start": v(41.08, -89.61) * mm, "end": v(41.39, -89.6) * mm});
            skLineSegment(sketch, "E1088", {"start": v(41.39, -89.6) * mm, "end": v(41.7, -89.57) * mm});
            skLineSegment(sketch, "E1089", {"start": v(41.7, -89.57) * mm, "end": v(42, -89.5) * mm});
            skLineSegment(sketch, "E1090", {"start": v(42, -89.5) * mm, "end": v(42.29, -89.42) * mm});
            skLineSegment(sketch, "E1091", {"start": v(42.29, -89.42) * mm, "end": v(42.58, -89.3) * mm});
            skLineSegment(sketch, "E1092", {"start": v(42.58, -89.3) * mm, "end": v(42.88, -89.13) * mm});
            skLineSegment(sketch, "E1093", {"start": v(42.88, -89.13) * mm, "end": v(43.18, -88.94) * mm});
            skLineSegment(sketch, "E1094", {"start": v(43.18, -88.94) * mm, "end": v(43.49, -88.7) * mm});
            skLineSegment(sketch, "E1095", {"start": v(43.49, -88.7) * mm, "end": v(45.1, -87.78) * mm});
            skLineSegment(sketch, "E1096", {"start": v(45.1, -87.78) * mm, "end": v(49.92, -87.78) * mm});
            skLineSegment(sketch, "E1097", {"start": v(49.92, -87.78) * mm, "end": v(54.74, -89.61) * mm});
            skLineSegment(sketch, "E1098", {"start": v(54.74, -89.61) * mm, "end": v(55.2, -89.69) * mm});
            skLineSegment(sketch, "E1099", {"start": v(55.2, -89.69) * mm, "end": v(55.66, -89.73) * mm});
            skLineSegment(sketch, "E1100", {"start": v(55.66, -89.73) * mm, "end": v(56.12, -89.74) * mm});
            skLineSegment(sketch, "E1101", {"start": v(56.12, -89.74) * mm, "end": v(56.57, -89.72) * mm});
            skLineSegment(sketch, "E1102", {"start": v(56.57, -89.72) * mm, "end": v(57.03, -89.67) * mm});
            skLineSegment(sketch, "E1103", {"start": v(57.03, -89.67) * mm, "end": v(57.49, -89.6) * mm});
            skLineSegment(sketch, "E1104", {"start": v(57.49, -89.6) * mm, "end": v(57.94, -89.5) * mm});
            skLineSegment(sketch, "E1105", {"start": v(57.94, -89.5) * mm, "end": v(58.4, -89.38) * mm});
            skLineSegment(sketch, "E1106", {"start": v(58.4, -89.38) * mm, "end": v(58.85, -89.23) * mm});
            skLineSegment(sketch, "E1107", {"start": v(58.85, -89.23) * mm, "end": v(59.3, -89.07) * mm});
            skLineSegment(sketch, "E1108", {"start": v(59.3, -89.07) * mm, "end": v(59.76, -88.9) * mm});
            skLineSegment(sketch, "E1109", {"start": v(59.76, -88.9) * mm, "end": v(60.2, -88.7) * mm});
            skLineSegment(sketch, "E1110", {"start": v(60.2, -88.7) * mm, "end": v(61.1, -88.26) * mm});
            skLineSegment(sketch, "E1111", {"start": v(61.1, -88.26) * mm, "end": v(61.98, -87.78) * mm});
            skLineSegment(sketch, "E1112", {"start": v(61.98, -87.78) * mm, "end": v(68.41, -77.68) * mm});
            skLineSegment(sketch, "E1113", {"start": v(68.41, -77.68) * mm, "end": v(68.7, -77.36) * mm});
            skLineSegment(sketch, "E1114", {"start": v(68.7, -77.36) * mm, "end": v(69, -77.06) * mm});
            skLineSegment(sketch, "E1115", {"start": v(69, -77.06) * mm, "end": v(69.32, -76.78) * mm});
            skLineSegment(sketch, "E1116", {"start": v(69.32, -76.78) * mm, "end": v(69.65, -76.5) * mm});
            skLineSegment(sketch, "E1117", {"start": v(69.65, -76.5) * mm, "end": v(69.98, -76.25) * mm});
            skLineSegment(sketch, "E1118", {"start": v(69.98, -76.25) * mm, "end": v(70.32, -76) * mm});
            skLineSegment(sketch, "E1119", {"start": v(70.32, -76) * mm, "end": v(71.03, -75.55) * mm});
            skLineSegment(sketch, "E1120", {"start": v(71.03, -75.55) * mm, "end": v(71.76, -75.13) * mm});
            skLineSegment(sketch, "E1121", {"start": v(71.76, -75.13) * mm, "end": v(72.5, -74.74) * mm});
            skLineSegment(sketch, "E1122", {"start": v(72.5, -74.74) * mm, "end": v(73.27, -74.37) * mm});
            skLineSegment(sketch, "E1123", {"start": v(73.27, -74.37) * mm, "end": v(74.04, -74.01) * mm});
            skLineSegment(sketch, "E1124", {"start": v(74.04, -74.01) * mm, "end": v(84.5, -70.34) * mm});
            skLineSegment(sketch, "E1125", {"start": v(84.5, -70.34) * mm, "end": v(85.67, -69.55) * mm});
            skLineSegment(sketch, "E1126", {"start": v(85.67, -69.55) * mm, "end": v(86.84, -68.74) * mm});
            skLineSegment(sketch, "E1127", {"start": v(86.84, -68.74) * mm, "end": v(87.99, -67.9) * mm});
            skLineSegment(sketch, "E1128", {"start": v(87.99, -67.9) * mm, "end": v(89.12, -67.02) * mm});
            skLineSegment(sketch, "E1129", {"start": v(89.12, -67.02) * mm, "end": v(90.22, -66.1) * mm});
            skLineSegment(sketch, "E1130", {"start": v(90.22, -66.1) * mm, "end": v(90.76, -65.61) * mm});
            skLineSegment(sketch, "E1131", {"start": v(90.76, -65.61) * mm, "end": v(91.3, -65.12) * mm});
            skLineSegment(sketch, "E1132", {"start": v(91.3, -65.12) * mm, "end": v(91.82, -64.61) * mm});
            skLineSegment(sketch, "E1133", {"start": v(91.82, -64.61) * mm, "end": v(92.33, -64.09) * mm});
            skLineSegment(sketch, "E1134", {"start": v(92.33, -64.09) * mm, "end": v(92.84, -63.55) * mm});
            skLineSegment(sketch, "E1135", {"start": v(92.84, -63.55) * mm, "end": v(93.34, -63) * mm});
            skLineSegment(sketch, "E1136", {"start": v(93.34, -63) * mm, "end": v(93.8, -62.44) * mm});
            skLineSegment(sketch, "E1137", {"start": v(93.8, -62.44) * mm, "end": v(94.23, -61.86) * mm});
            skLineSegment(sketch, "E1138", {"start": v(94.23, -61.86) * mm, "end": v(94.63, -61.25) * mm});
            skLineSegment(sketch, "E1139", {"start": v(94.63, -61.25) * mm, "end": v(95, -60.61) * mm});
            skLineSegment(sketch, "E1140", {"start": v(95, -60.61) * mm, "end": v(95.35, -59.96) * mm});
            skLineSegment(sketch, "E1141", {"start": v(95.35, -59.96) * mm, "end": v(95.67, -59.29) * mm});
            skLineSegment(sketch, "E1142", {"start": v(95.67, -59.29) * mm, "end": v(95.98, -58.6) * mm});
            skLineSegment(sketch, "E1143", {"start": v(95.98, -58.6) * mm, "end": v(96.27, -57.9) * mm});
            skLineSegment(sketch, "E1144", {"start": v(96.27, -57.9) * mm, "end": v(96.54, -57.18) * mm});
            skLineSegment(sketch, "E1145", {"start": v(96.54, -57.18) * mm, "end": v(96.8, -56.45) * mm});
            skLineSegment(sketch, "E1146", {"start": v(96.8, -56.45) * mm, "end": v(97.27, -54.98) * mm});
            skLineSegment(sketch, "E1147", {"start": v(97.27, -54.98) * mm, "end": v(97.73, -53.48) * mm});
            skLineSegment(sketch, "E1148", {"start": v(97.73, -53.48) * mm, "end": v(98.16, -51.98) * mm});
            skLineSegment(sketch, "E1149", {"start": v(98.16, -51.98) * mm, "end": v(98.23, -51.3) * mm});
            skLineSegment(sketch, "E1150", {"start": v(98.23, -51.3) * mm, "end": v(98.29, -50.61) * mm});
            skLineSegment(sketch, "E1151", {"start": v(98.29, -50.61) * mm, "end": v(98.32, -49.93) * mm});
            skLineSegment(sketch, "E1152", {"start": v(98.32, -49.93) * mm, "end": v(98.35, -49.24) * mm});
            skLineSegment(sketch, "E1153", {"start": v(98.35, -49.24) * mm, "end": v(98.35, -47.87) * mm});
            skLineSegment(sketch, "E1154", {"start": v(98.35, -47.87) * mm, "end": v(98.33, -46.49) * mm});
            skLineSegment(sketch, "E1155", {"start": v(98.33, -46.49) * mm, "end": v(98.22, -43.73) * mm});
            skLineSegment(sketch, "E1156", {"start": v(98.22, -43.73) * mm, "end": v(98.18, -42.35) * mm});
            skLineSegment(sketch, "E1157", {"start": v(98.18, -42.35) * mm, "end": v(98.16, -40.97) * mm});
            skLineSegment(sketch, "E1158", {"start": v(98.16, -40.97) * mm, "end": v(96.88, -38.8) * mm});
            skLineSegment(sketch, "E1159", {"start": v(96.88, -38.8) * mm, "end": v(96.21, -37.74) * mm});
            skLineSegment(sketch, "E1160", {"start": v(96.21, -37.74) * mm, "end": v(95.53, -36.68) * mm});
            skLineSegment(sketch, "E1161", {"start": v(95.53, -36.68) * mm, "end": v(94.83, -35.65) * mm});
            skLineSegment(sketch, "E1162", {"start": v(94.83, -35.65) * mm, "end": v(94.1, -34.64) * mm});
            skLineSegment(sketch, "E1163", {"start": v(94.1, -34.64) * mm, "end": v(93.34, -33.66) * mm});
            skLineSegment(sketch, "E1164", {"start": v(93.34, -33.66) * mm, "end": v(92.53, -32.7) * mm});
            skCircle(sketch, "E1165", {"center": v(33.83, 9.87) * mm, "radius": 27.53 * mm});
            skSolve(sketch);
        }
        {
            var Q0;
            Q0 = qSketchRegion(id + "F0", true);
            extrude(context, id + "F1", {"entities" : qUnion([Q0]), "depth" : 3 * mm, "offsetDistance" : 25 * mm});
        }
    });
